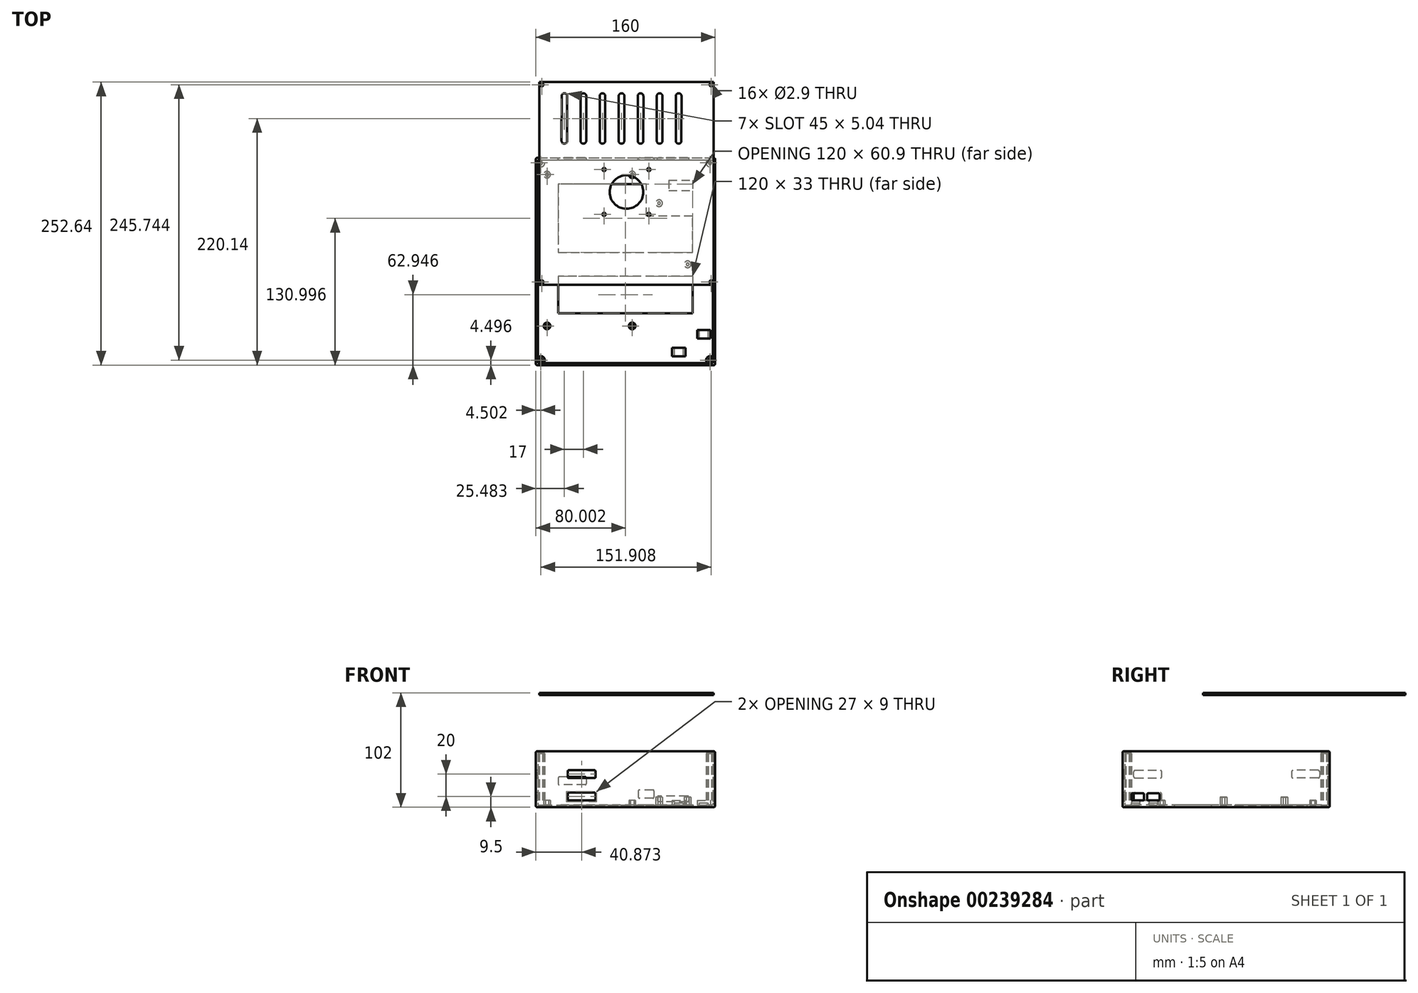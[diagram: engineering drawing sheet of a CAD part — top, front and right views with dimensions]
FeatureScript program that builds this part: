
annotation { "Feature Type Name" : "Feature", "Feature Type Description" : "" }
export const myFeature = defineFeature(function(context is Context, id is Id, definition is map)
    precondition{}
    {
        {
            assignVariable(context, id + "F0", {"name" : "mksPoleHeight", "anyValue" : 6});
        }
        {
            assignVariable(context, id + "F1", {"name" : "rpiPoleHeight", "anyValue" : 9});
        }
        {
            assignVariable(context, id + "F2", {"name" : "outerPoleHeight", "anyValue" : 48});
        }
        {
            var Q0;
            Q0=qCreatedBy(makeId("Top.planeOp"),FACE);
            var sketch = newSketch(context, id + "F3", { "sketchPlane" : qUnion([Q0])});
            skLineSegment(sketch, "E0.bottom", {"start": v(24.93, -36.84) * mm, "end": v(-51.07, -36.84) * mm});
            skLineSegment(sketch, "E0.top", {"start": v(24.93, 98.16) * mm, "end": v(-51.07, 98.16) * mm});
            skLineSegment(sketch, "E0.left", {"start": v(24.93, -36.84) * mm, "end": v(24.93, 98.16) * mm});
            skLineSegment(sketch, "E0.right", {"start": v(-51.07, -36.84) * mm, "end": v(-51.07, 98.16) * mm});
            skPoint(sketch, "E1", {"position": v(24.93, -36.84) * mm});
            skPoint(sketch, "E2", {"position": v(-51.07, -36.84) * mm});
            skPoint(sketch, "E3", {"position": v(24.93, 98.16) * mm});
            skPoint(sketch, "E4", {"position": v(-51.07, 98.16) * mm});
            skCircle(sketch, "E5", {"center": v(-51.07, 98.16) * mm, "radius": 3 * mm});
            skCircle(sketch, "E6", {"center": v(-51.07, -36.84) * mm, "radius": 3 * mm});
            skCircle(sketch, "E7", {"center": v(24.93, -36.84) * mm, "radius": 3 * mm});
            skCircle(sketch, "E8", {"center": v(24.93, 98.16) * mm, "radius": 3 * mm});
            skSolve(sketch);
        }
        {
            var Q0;
            {var subQ0=sQuery(id+"F3.wireOp",EDGE,"E7");var subQ1=sQuery(id+"F3.wireOp",EDGE,"E0.bottom");var subQ2=makeQuery(id+"F3.imprint","INTERSECT",VERTEX,{"derivedFrom":[subQ1,subQ0]});Q0=makeQuery(id+"F3.imprint","IMPRINT",FACE,{"disambiguationData":[TD([[makeQuery(id+"F3.imprint","IMPRINT",EDGE,{"disambiguationData":[TD([[subQ2,1.0]])],"derivedFrom":subQ1}),1.0]])]});}
            var Q1;
            {var subQ0=sQuery(id+"F3.wireOp",EDGE,"E7");var subQ1=sQuery(id+"F3.wireOp",EDGE,"E0.bottom");var subQ2=makeQuery(id+"F3.imprint","INTERSECT",VERTEX,{"derivedFrom":[subQ1,subQ0]});Q1=makeQuery(id+"F3.imprint","IMPRINT",FACE,{"disambiguationData":[TD([[makeQuery(id+"F3.imprint","IMPRINT",EDGE,{"disambiguationData":[TD([[subQ2,1.0]])],"derivedFrom":subQ1}),-1.0]])]});}
            var Q2;
            {var subQ0=sQuery(id+"F3.wireOp",EDGE,"E8");var subQ1=sQuery(id+"F3.wireOp",EDGE,"E0.top");var subQ2=makeQuery(id+"F3.imprint","INTERSECT",VERTEX,{"derivedFrom":[subQ1,subQ0]});Q2=makeQuery(id+"F3.imprint","IMPRINT",FACE,{"disambiguationData":[TD([[makeQuery(id+"F3.imprint","IMPRINT",EDGE,{"disambiguationData":[TD([[subQ2,1.0]])],"derivedFrom":subQ1}),1.0]])]});}
            var Q3;
            {var subQ0=sQuery(id+"F3.wireOp",EDGE,"E8");var subQ1=sQuery(id+"F3.wireOp",EDGE,"E0.top");var subQ2=makeQuery(id+"F3.imprint","INTERSECT",VERTEX,{"derivedFrom":[subQ1,subQ0]});Q3=makeQuery(id+"F3.imprint","IMPRINT",FACE,{"disambiguationData":[TD([[makeQuery(id+"F3.imprint","IMPRINT",EDGE,{"disambiguationData":[TD([[subQ2,1.0]])],"derivedFrom":subQ1}),-1.0]])]});}
            var Q4;
            {var subQ0=sQuery(id+"F3.wireOp",EDGE,"E5");var subQ1=sQuery(id+"F3.wireOp",EDGE,"E0.top");var subQ2=makeQuery(id+"F3.imprint","INTERSECT",VERTEX,{"derivedFrom":[subQ1,subQ0]});Q4=makeQuery(id+"F3.imprint","IMPRINT",FACE,{"disambiguationData":[TD([[makeQuery(id+"F3.imprint","IMPRINT",EDGE,{"disambiguationData":[TD([[subQ2,-1.0]])],"derivedFrom":subQ1}),-1.0]])]});}
            var Q5;
            {var subQ0=sQuery(id+"F3.wireOp",EDGE,"E5");var subQ1=sQuery(id+"F3.wireOp",EDGE,"E0.top");var subQ2=makeQuery(id+"F3.imprint","INTERSECT",VERTEX,{"derivedFrom":[subQ1,subQ0]});Q5=makeQuery(id+"F3.imprint","IMPRINT",FACE,{"disambiguationData":[TD([[makeQuery(id+"F3.imprint","IMPRINT",EDGE,{"disambiguationData":[TD([[subQ2,-1.0]])],"derivedFrom":subQ1}),1.0]])]});}
            var Q6;
            {var subQ0=sQuery(id+"F3.wireOp",EDGE,"E6");var subQ1=sQuery(id+"F3.wireOp",EDGE,"E0.bottom");var subQ2=makeQuery(id+"F3.imprint","INTERSECT",VERTEX,{"derivedFrom":[subQ1,subQ0]});Q6=makeQuery(id+"F3.imprint","IMPRINT",FACE,{"disambiguationData":[TD([[makeQuery(id+"F3.imprint","IMPRINT",EDGE,{"disambiguationData":[TD([[subQ2,-1.0]])],"derivedFrom":subQ1}),-1.0]])]});}
            var Q7;
            {var subQ0=sQuery(id+"F3.wireOp",EDGE,"E6");var subQ1=sQuery(id+"F3.wireOp",EDGE,"E0.bottom");var subQ2=makeQuery(id+"F3.imprint","INTERSECT",VERTEX,{"derivedFrom":[subQ1,subQ0]});Q7=makeQuery(id+"F3.imprint","IMPRINT",FACE,{"disambiguationData":[TD([[makeQuery(id+"F3.imprint","IMPRINT",EDGE,{"disambiguationData":[TD([[subQ2,-1.0]])],"derivedFrom":subQ1}),1.0]])]});}
            extrude(context, id + "F4", {"entities" : qUnion([Q0, Q1, Q2, Q3, Q4, Q5, Q6, Q7]), "depth" : getVariable(context, 'mksPoleHeight') * mm});
        }
        {
            var Q0;
            Q0=qCreatedBy(makeId("Top.planeOp"),FACE);
            var sketch = newSketch(context, id + "F5", { "sketchPlane" : qUnion([Q0])});
            skLineSegment(sketch, "E9.bottom", {"start": v(86.93, 13.16) * mm, "end": v(30.93, 13.16) * mm});
            skLineSegment(sketch, "E9.top", {"start": v(86.93, 98.16) * mm, "end": v(30.93, 98.16) * mm});
            skLineSegment(sketch, "E9.left", {"start": v(86.93, 13.16) * mm, "end": v(86.93, 98.16) * mm});
            skLineSegment(sketch, "E9.right", {"start": v(30.93, 13.16) * mm, "end": v(30.93, 98.16) * mm});
            skPoint(sketch, "E10", {"position": v(74.43, 18.16) * mm});
            skPoint(sketch, "E11", {"position": v(48.93, 72.66) * mm});
            skCircle(sketch, "E12", {"center": v(48.93, 72.66) * mm, "radius": 3 * mm});
            skCircle(sketch, "E13", {"center": v(74.43, 18.16) * mm, "radius": 3 * mm});
            skSolve(sketch);
        }
        {
            var Q0;
            Q0=makeQuery(id+"F5.imprint","IMPRINT",FACE,{"disambiguationData":[TD([[makeQuery(id+"F5.imprint","IMPRINT",EDGE,{"derivedFrom":sQuery(id+"F5.wireOp",EDGE,"E13")}),1.0]])]});
            var Q1;
            Q1=makeQuery(id+"F5.imprint","IMPRINT",FACE,{"disambiguationData":[TD([[makeQuery(id+"F5.imprint","IMPRINT",EDGE,{"derivedFrom":sQuery(id+"F5.wireOp",EDGE,"E12")}),1.0]])]});
            extrude(context, id + "F6", {"entities" : qUnion([Q0, Q1]), "depth" : getVariable(context, 'rpiPoleHeight') * mm});
        }
        {
            var Q0;
            Q0=qCreatedBy(makeId("Top.planeOp"),FACE);
            var sketch = newSketch(context, id + "F7", { "sketchPlane" : qUnion([Q0])});
            skLineSegment(sketch, "E14.bottom", {"start": v(-61.07, 113.16) * mm, "end": v(98.93, 113.16) * mm});
            skLineSegment(sketch, "E14.top", {"start": v(-61.07, -71.84) * mm, "end": v(98.93, -71.84) * mm});
            skLineSegment(sketch, "E14.left", {"start": v(-61.07, 113.16) * mm, "end": v(-61.07, -71.84) * mm});
            skLineSegment(sketch, "E14.right", {"start": v(98.93, 113.16) * mm, "end": v(98.93, -71.84) * mm});
            skPoint(sketch, "E15", {"position": v(-56.57, 108.66) * mm});
            skPoint(sketch, "E16", {"position": v(-56.57, -67.34) * mm});
            skPoint(sketch, "E17", {"position": v(94.43, -67.34) * mm});
            skPoint(sketch, "E18", {"position": v(94.43, 108.66) * mm});
            skCircle(sketch, "E19", {"center": v(-56.57, -67.34) * mm, "radius": 3.5 * mm});
            skCircle(sketch, "E20", {"center": v(94.43, -67.34) * mm, "radius": 3.5 * mm});
            skCircle(sketch, "E21", {"center": v(94.43, 108.66) * mm, "radius": 3.5 * mm});
            skCircle(sketch, "E22", {"center": v(-56.57, 108.66) * mm, "radius": 3.5 * mm});
            skSolve(sketch);
        }
        {
            var Q0;
            Q0=makeQuery(id+"F7.imprint","IMPRINT",FACE,{"disambiguationData":[TD([[makeQuery(id+"F7.imprint","IMPRINT",EDGE,{"derivedFrom":sQuery(id+"F7.wireOp",EDGE,"E14.bottom")}),-1.0]])]});
            var Q1;
            Q1=makeQuery(id+"F7.imprint","IMPRINT",FACE,{"disambiguationData":[TD([[makeQuery(id+"F7.imprint","IMPRINT",EDGE,{"derivedFrom":sQuery(id+"F7.wireOp",EDGE,"E22")}),1.0]])]});
            var Q2;
            Q2=makeQuery(id+"F7.imprint","IMPRINT",FACE,{"disambiguationData":[TD([[makeQuery(id+"F7.imprint","IMPRINT",EDGE,{"derivedFrom":sQuery(id+"F7.wireOp",EDGE,"E19")}),1.0]])]});
            var Q3;
            Q3=makeQuery(id+"F7.imprint","IMPRINT",FACE,{"disambiguationData":[TD([[makeQuery(id+"F7.imprint","IMPRINT",EDGE,{"derivedFrom":sQuery(id+"F7.wireOp",EDGE,"E20")}),1.0]])]});
            var Q4;
            Q4=makeQuery(id+"F7.imprint","IMPRINT",FACE,{"disambiguationData":[TD([[makeQuery(id+"F7.imprint","IMPRINT",EDGE,{"derivedFrom":sQuery(id+"F7.wireOp",EDGE,"E21")}),1.0]])]});
            extrude(context, id + "F8", {"entities" : qUnion([Q0, Q1, Q2, Q3, Q4]), "depth" : 50 * mm});
        }
        {
            var Q0;
            Q0=makeQuery(id+"F8.opExtrude","CAP_FACE",FACE,{"disambiguationData":[OSD([sQuery(id+"F7.wireOp",EDGE,"E14.bottom"),sQuery(id+"F7.wireOp",EDGE,"E14.top"),sQuery(id+"F7.wireOp",EDGE,"E14.left"),sQuery(id+"F7.wireOp",EDGE,"E14.right")])],"isStart":false});
            shell(context, id + "F9", {"entities" : qUnion([Q0]), "thickness" : 2 * mm});
        }
        {
            var Q0;
            Q0=makeQuery(id+"F7.imprint","IMPRINT",FACE,{"disambiguationData":[TD([[makeQuery(id+"F7.imprint","IMPRINT",EDGE,{"derivedFrom":sQuery(id+"F7.wireOp",EDGE,"E19")}),1.0]])]});
            var Q1;
            Q1=makeQuery(id+"F7.imprint","IMPRINT",FACE,{"disambiguationData":[TD([[makeQuery(id+"F7.imprint","IMPRINT",EDGE,{"derivedFrom":sQuery(id+"F7.wireOp",EDGE,"E20")}),1.0]])]});
            var Q2;
            Q2=makeQuery(id+"F7.imprint","IMPRINT",FACE,{"disambiguationData":[TD([[makeQuery(id+"F7.imprint","IMPRINT",EDGE,{"derivedFrom":sQuery(id+"F7.wireOp",EDGE,"E21")}),1.0]])]});
            var Q3;
            Q3=makeQuery(id+"F7.imprint","IMPRINT",FACE,{"disambiguationData":[TD([[makeQuery(id+"F7.imprint","IMPRINT",EDGE,{"derivedFrom":sQuery(id+"F7.wireOp",EDGE,"E22")}),1.0]])]});
            var Q4;
            Q4=sQuery(id+"F7.wireOp",EDGE,"E19");
            var Q5;
            Q5=sQuery(id+"F7.wireOp",EDGE,"E20");
            var Q6;
            Q6=sQuery(id+"F7.wireOp",EDGE,"E21");
            var Q7;
            Q7=sQuery(id+"F7.wireOp",EDGE,"E22");
            extrude(context, id + "F10", {"entities" : qUnion([Q0, Q1, Q2, Q3]), "surfaceEntities" : qUnion([Q4, Q5, Q6, Q7]), "depth" : (getVariable(context, 'outerPoleHeight')) * mm});
        }
        {
            var Q0;
            Q0=makeQuery(id+"F8.opExtrude","CAP_FACE",FACE,{"disambiguationData":[OSD([sQuery(id+"F7.wireOp",EDGE,"E14.bottom"),sQuery(id+"F7.wireOp",EDGE,"E14.top"),sQuery(id+"F7.wireOp",EDGE,"E14.left"),sQuery(id+"F7.wireOp",EDGE,"E14.right")])],"isStart":false});
            cPlane(context, id + "F11", {"entities" : qUnion([Q0]), "cplaneType" : CPlaneType.OFFSET, "offset" : 0 * mm, "width" : 150 * mm, "height" : 150 * mm});
        }
        {
            var Q0;
            Q0=qCreatedBy(id+"F11.planeOp",FACE);
            var sketch = newSketch(context, id + "F12", { "sketchPlane" : qUnion([Q0])});
            skLineSegment(sketch, "E23.bottom", {"start": v(-59.07, 111.16) * mm, "end": v(96.93, 111.16) * mm});
            skLineSegment(sketch, "E23.top", {"start": v(-59.07, -69.84) * mm, "end": v(96.93, -69.84) * mm});
            skLineSegment(sketch, "E23.left", {"start": v(-59.07, 111.16) * mm, "end": v(-59.07, -69.84) * mm});
            skLineSegment(sketch, "E23.right", {"start": v(96.93, 111.16) * mm, "end": v(96.93, -69.84) * mm});
            skSolve(sketch);
        }
        {
            var Q0;
            Q0=makeQuery(id+"F12.imprint","IMPRINT",FACE,{"disambiguationData":[TD([[makeQuery(id+"F12.imprint","IMPRINT",EDGE,{"derivedFrom":sQuery(id+"F12.wireOp",EDGE,"E23.bottom")}),-1.0]])]});
            extrude(context, id + "F13", {"entities" : qUnion([Q0]), "operationType" : NewBodyOperationType.REMOVE, "oppositeDirection" : true, "depth" : 2 * mm});
        }
        {
            var Q0;
            Q0=makeQuery(id+"F4.opExtrude","SWEPT_BODY",BODY,{"disambiguationData":[OSD([sQuery(id+"F3.wireOp",EDGE,"E5")])]});
            var Q1;
            Q1=makeQuery(id+"F4.opExtrude","SWEPT_BODY",BODY,{"disambiguationData":[OSD([sQuery(id+"F3.wireOp",EDGE,"E6")])]});
            var Q2;
            Q2=makeQuery(id+"F4.opExtrude","SWEPT_BODY",BODY,{"disambiguationData":[OSD([sQuery(id+"F3.wireOp",EDGE,"E7")])]});
            var Q3;
            Q3=makeQuery(id+"F4.opExtrude","SWEPT_BODY",BODY,{"disambiguationData":[OSD([sQuery(id+"F3.wireOp",EDGE,"E8")])]});
            var Q4;
            Q4=makeQuery(id+"F6.opExtrude","SWEPT_BODY",BODY,{"disambiguationData":[OSD([sQuery(id+"F5.wireOp",EDGE,"E12")])]});
            var Q5;
            Q5=makeQuery(id+"F6.opExtrude","SWEPT_BODY",BODY,{"disambiguationData":[OSD([sQuery(id+"F5.wireOp",EDGE,"E13")])]});
            var Q6;
            Q6=makeQuery(id+"F8.opExtrude","SWEPT_BODY",BODY,{"disambiguationData":[OSD([sQuery(id+"F7.wireOp",EDGE,"E14.bottom"),sQuery(id+"F7.wireOp",EDGE,"E14.top"),sQuery(id+"F7.wireOp",EDGE,"E14.left"),sQuery(id+"F7.wireOp",EDGE,"E14.right")])]});
            var Q7;
            Q7=makeQuery(id+"F10.opExtrude","SWEPT_BODY",BODY,{"disambiguationData":[OSD([sQuery(id+"F7.wireOp",EDGE,"E19")])]});
            var Q8;
            Q8=makeQuery(id+"F10.opExtrude","SWEPT_BODY",BODY,{"disambiguationData":[OSD([sQuery(id+"F7.wireOp",EDGE,"E20")])]});
            var Q9;
            Q9=makeQuery(id+"F10.opExtrude","SWEPT_BODY",BODY,{"disambiguationData":[OSD([sQuery(id+"F7.wireOp",EDGE,"E21")])]});
            var Q10;
            Q10=makeQuery(id+"F10.opExtrude","SWEPT_BODY",BODY,{"disambiguationData":[OSD([sQuery(id+"F7.wireOp",EDGE,"E22")])]});
            booleanBodies(context, id + "F14", {"operationType" : BooleanOperationType.UNION, "tools" : qUnion([Q0, Q1, Q2, Q3, Q4, Q5, Q6, Q7, Q8, Q9, Q10])});
        }
        {
            var Q0;
            Q0=sQuery(id+"F7.wireOp",VERTEX,"E16");
            var Q1;
            Q1=sQuery(id+"F7.wireOp",VERTEX,"E15");
            var Q2;
            Q2=sQuery(id+"F7.wireOp",VERTEX,"E18");
            var Q3;
            Q3=sQuery(id+"F7.wireOp",VERTEX,"E17");
            var Q4;
            Q4=sQuery(id+"F3.wireOp",VERTEX,"E3");
            var Q5;
            Q5=sQuery(id+"F3.wireOp",VERTEX,"E4");
            var Q6;
            Q6=sQuery(id+"F3.wireOp",VERTEX,"E2");
            var Q7;
            Q7=sQuery(id+"F3.wireOp",VERTEX,"E1");
            var Q8;
            Q8=makeQuery(id+"F4.opExtrude","SWEPT_BODY",BODY,{"disambiguationData":[OSD([sQuery(id+"F3.wireOp",EDGE,"E5")])]});
            hole(context, id + "F15", {"style" : HoleStyle.SIMPLE, "endStyle" : HoleEndStyle.THROUGH, "oppositeDirection" : true, "holeDiameter" : 2.9 * mm, "tappedDepth" : 12 * mm, "tapClearance" : 3, "startFromSketch" : true, "locations" : qUnion([Q0, Q1, Q2, Q3, Q4, Q5, Q6, Q7]), "scope" : qUnion([Q8])});
        }
        {
            var Q0;
            Q0=qCreatedBy(id+"F11.planeOp",FACE);
            cPlane(context, id + "F16", {"entities" : qUnion([Q0]), "cplaneType" : CPlaneType.OFFSET, "offset" : 50 * mm, "width" : 150 * mm, "height" : 150 * mm});
        }
        {
            var Q0;
            Q0=qCreatedBy(id+"F16.planeOp",FACE);
            var sketch = newSketch(context, id + "F17", { "sketchPlane" : qUnion([Q0])});
            skLineSegment(sketch, "E24.bottom", {"start": v(-58.06, 180.8) * mm, "end": v(97.74, 180.8) * mm});
            skLineSegment(sketch, "E24.top", {"start": v(-58.06, 0) * mm, "end": v(97.74, 0) * mm});
            skLineSegment(sketch, "E24.left", {"start": v(-58.06, 180.8) * mm, "end": v(-58.06, 0) * mm});
            skLineSegment(sketch, "E24.right", {"start": v(97.74, 180.8) * mm, "end": v(97.74, 0) * mm});
            skPoint(sketch, "E25", {"position": v(-55.66, 178.4) * mm});
            skPoint(sketch, "E26", {"position": v(95.34, 178.4) * mm});
            skPoint(sketch, "E27", {"position": v(95.34, 2.4) * mm});
            skPoint(sketch, "E28", {"position": v(-55.66, 2.4) * mm});
            skCircle(sketch, "E29", {"center": v(-55.66, 178.4) * mm, "radius": 1.45 * mm});
            skCircle(sketch, "E30", {"center": v(95.34, 178.4) * mm, "radius": 1.45 * mm});
            skCircle(sketch, "E31", {"center": v(95.34, 2.4) * mm, "radius": 1.45 * mm});
            skCircle(sketch, "E32", {"center": v(-55.66, 2.4) * mm, "radius": 1.45 * mm});
            skArc(sketch, "E33.0.startCap", {"start": v(-38.06, 168.3) * mm, "mid": v(-35.56, 170.8) * mm, "end": v(-33.07, 168.3) * mm});
            skArc(sketch, "E33.0.endCap", {"start": v(-33.1, 128.3) * mm, "mid": v(-35.61, 125.8) * mm, "end": v(-38.1, 128.3) * mm});
            skLineSegment(sketch, "E33.0.left", {"start": v(-33.07, 168.3) * mm, "end": v(-33.1, 128.3) * mm});
            skLineSegment(sketch, "E33.0.right", {"start": v(-38.06, 168.3) * mm, "end": v(-38.1, 128.3) * mm});
            skArc(sketch, "E34.0.startCap", {"start": v(-21.06, 168.3) * mm, "mid": v(-18.56, 170.8) * mm, "end": v(-16.06, 168.3) * mm});
            skArc(sketch, "E34.0.endCap", {"start": v(-16.1, 128.3) * mm, "mid": v(-18.61, 125.8) * mm, "end": v(-21.1, 128.3) * mm});
            skLineSegment(sketch, "E34.0.left", {"start": v(-16.06, 168.3) * mm, "end": v(-16.1, 128.3) * mm});
            skLineSegment(sketch, "E34.0.right", {"start": v(-21.06, 168.3) * mm, "end": v(-21.1, 128.3) * mm});
            skArc(sketch, "E35.0.startCap", {"start": v(-4.06, 168.3) * mm, "mid": v(-1.56, 170.8) * mm, "end": v(0.94, 168.3) * mm});
            skArc(sketch, "E35.0.endCap", {"start": v(0.9, 128.3) * mm, "mid": v(-1.61, 125.8) * mm, "end": v(-4.1, 128.3) * mm});
            skLineSegment(sketch, "E35.0.left", {"start": v(0.94, 168.3) * mm, "end": v(0.9, 128.3) * mm});
            skLineSegment(sketch, "E35.0.right", {"start": v(-4.06, 168.3) * mm, "end": v(-4.1, 128.3) * mm});
            skArc(sketch, "E36.0.startCap", {"start": v(12.94, 168.3) * mm, "mid": v(15.44, 170.8) * mm, "end": v(17.94, 168.3) * mm});
            skArc(sketch, "E36.0.endCap", {"start": v(17.9, 128.3) * mm, "mid": v(15.39, 125.8) * mm, "end": v(12.9, 128.3) * mm});
            skLineSegment(sketch, "E36.0.left", {"start": v(17.94, 168.3) * mm, "end": v(17.9, 128.3) * mm});
            skLineSegment(sketch, "E36.0.right", {"start": v(12.94, 168.3) * mm, "end": v(12.9, 128.3) * mm});
            skArc(sketch, "E37.0.startCap", {"start": v(29.94, 168.3) * mm, "mid": v(32.44, 170.8) * mm, "end": v(34.94, 168.3) * mm});
            skArc(sketch, "E37.0.endCap", {"start": v(34.9, 128.3) * mm, "mid": v(32.39, 125.8) * mm, "end": v(29.9, 128.3) * mm});
            skLineSegment(sketch, "E37.0.left", {"start": v(34.94, 168.3) * mm, "end": v(34.9, 128.3) * mm});
            skLineSegment(sketch, "E37.0.right", {"start": v(29.94, 168.3) * mm, "end": v(29.9, 128.3) * mm});
            skArc(sketch, "E38.0.startCap", {"start": v(46.94, 168.3) * mm, "mid": v(49.44, 170.8) * mm, "end": v(51.94, 168.3) * mm});
            skArc(sketch, "E38.0.endCap", {"start": v(51.9, 128.3) * mm, "mid": v(49.39, 125.8) * mm, "end": v(46.9, 128.3) * mm});
            skLineSegment(sketch, "E38.0.left", {"start": v(51.94, 168.3) * mm, "end": v(51.9, 128.3) * mm});
            skLineSegment(sketch, "E38.0.right", {"start": v(46.94, 168.3) * mm, "end": v(46.9, 128.3) * mm});
            skArc(sketch, "E39.0.startCap", {"start": v(63.94, 168.3) * mm, "mid": v(66.44, 170.8) * mm, "end": v(68.94, 168.3) * mm});
            skArc(sketch, "E39.0.endCap", {"start": v(68.9, 128.3) * mm, "mid": v(66.39, 125.8) * mm, "end": v(63.9, 128.3) * mm});
            skLineSegment(sketch, "E39.0.left", {"start": v(68.94, 168.3) * mm, "end": v(68.9, 128.3) * mm});
            skLineSegment(sketch, "E39.0.right", {"start": v(63.94, 168.3) * mm, "end": v(63.9, 128.3) * mm});
            skPoint(sketch, "E40", {"position": v(19.84, 82.67) * mm});
            skCircle(sketch, "E41", {"center": v(19.84, 82.67) * mm, "radius": 15 * mm});
            skLineSegment(sketch, "E42.bottom", {"start": v(39.84, 102.67) * mm, "end": v(-0.16, 102.67) * mm});
            skLineSegment(sketch, "E42.top", {"start": v(39.84, 62.67) * mm, "end": v(-0.16, 62.67) * mm});
            skLineSegment(sketch, "E42.left", {"start": v(39.84, 102.67) * mm, "end": v(39.84, 62.67) * mm});
            skLineSegment(sketch, "E42.right", {"start": v(-0.16, 102.67) * mm, "end": v(-0.16, 62.67) * mm});
            skCircle(sketch, "E43", {"center": v(-0.16, 102.67) * mm, "radius": 1.45 * mm});
            skCircle(sketch, "E44", {"center": v(-0.16, 62.67) * mm, "radius": 1.45 * mm});
            skCircle(sketch, "E45", {"center": v(39.84, 102.67) * mm, "radius": 1.45 * mm});
            skCircle(sketch, "E46", {"center": v(39.84, 62.67) * mm, "radius": 1.45 * mm});
            skSolve(sketch);
        }
        {
            var Q0;
            Q0=makeQuery(id+"F17.imprint","IMPRINT",FACE,{"disambiguationData":[TD([[makeQuery(id+"F17.imprint","IMPRINT",EDGE,{"derivedFrom":sQuery(id+"F17.wireOp",EDGE,"E24.bottom")}),-1.0]])]});
            var Q1;
            Q1=makeQuery(id+"F17.imprint","IMPRINT",FACE,{"disambiguationData":[TD([[makeQuery(id+"F17.imprint","IMPRINT",EDGE,{"derivedFrom":sQuery(id+"F17.wireOp",EDGE,"E41")}),-1.0]])]});
            extrude(context, id + "F18", {"entities" : qUnion([Q0, Q1]), "depth" : 2 * mm});
        }
        {
            var Q0;
            Q0=makeQuery(id+"F8.opExtrude","SWEPT_FACE",FACE,{"disambiguationData":[OSD([sQuery(id+"F7.wireOp",EDGE,"E14.left")])]});
            var sketch = newSketch(context, id + "F19", { "sketchPlane" : qUnion([Q0])});
            skLineSegment(sketch, "E47.bottom", {"start": v(-79.13, 26) * mm, "end": v(-104.13, 26) * mm});
            skLineSegment(sketch, "E47.top", {"start": v(-79.13, 33) * mm, "end": v(-104.13, 33) * mm});
            skLineSegment(sketch, "E47.left", {"start": v(-79.13, 26) * mm, "end": v(-79.13, 33) * mm});
            skLineSegment(sketch, "E47.right", {"start": v(-104.13, 26) * mm, "end": v(-104.13, 33) * mm});
            skLineSegment(sketch, "E48.bottom", {"start": v(36.84, 33) * mm, "end": v(61.84, 33) * mm});
            skLineSegment(sketch, "E48.top", {"start": v(36.84, 26) * mm, "end": v(61.84, 26) * mm});
            skLineSegment(sketch, "E48.left", {"start": v(36.84, 33) * mm, "end": v(36.84, 26) * mm});
            skLineSegment(sketch, "E48.right", {"start": v(61.84, 33) * mm, "end": v(61.84, 26) * mm});
            skLineSegment(sketch, "E49.bottom", {"start": v(36.84, 13) * mm, "end": v(61.84, 13) * mm});
            skLineSegment(sketch, "E49.top", {"start": v(36.84, 6) * mm, "end": v(61.84, 6) * mm});
            skLineSegment(sketch, "E49.left", {"start": v(36.84, 13) * mm, "end": v(36.84, 6) * mm});
            skLineSegment(sketch, "E49.right", {"start": v(61.84, 13) * mm, "end": v(61.84, 6) * mm});
            skSolve(sketch);
        }
        {
            var Q0;
            Q0=makeQuery(id+"F19.imprint","IMPRINT",FACE,{"disambiguationData":[TD([[makeQuery(id+"F19.imprint","IMPRINT",EDGE,{"derivedFrom":sQuery(id+"F19.wireOp",EDGE,"E48.bottom")}),-1.0]])]});
            var Q1;
            Q1=makeQuery(id+"F19.imprint","IMPRINT",FACE,{"disambiguationData":[TD([[makeQuery(id+"F19.imprint","IMPRINT",EDGE,{"derivedFrom":sQuery(id+"F19.wireOp",EDGE,"d830608d-766a-4a5a-9b51-aef29d65a364.bottom")}),-1.0]])]});
            var Q2;
            Q2=makeQuery(id+"F19.imprint","IMPRINT",FACE,{"disambiguationData":[TD([[makeQuery(id+"F19.imprint","IMPRINT",EDGE,{"derivedFrom":sQuery(id+"F19.wireOp",EDGE,"E49.bottom")}),-1.0]])]});
            var Q3;
            Q3=makeQuery(id+"F19.imprint","IMPRINT",FACE,{"disambiguationData":[TD([[makeQuery(id+"F19.imprint","IMPRINT",EDGE,{"derivedFrom":sQuery(id+"F19.wireOp",EDGE,"E47.bottom")}),-1.0]])]});
            extrude(context, id + "F20", {"entities" : qUnion([Q0, Q1, Q2, Q3]), "operationType" : NewBodyOperationType.REMOVE, "oppositeDirection" : true, "depth" : 5 * mm});
        }
        {
            var Q0;
            Q0=makeQuery(id+"F8.opExtrude","SWEPT_FACE",FACE,{"disambiguationData":[OSD([sQuery(id+"F7.wireOp",EDGE,"E14.left")])]});
            var Q1;
            Q1=makeQuery(id+"F8.opExtrude","SWEPT_FACE",FACE,{"disambiguationData":[OSD([sQuery(id+"F7.wireOp",EDGE,"E14.bottom")])]});
            var Q2;
            Q2=makeQuery(id+"F8.opExtrude","SWEPT_FACE",FACE,{"disambiguationData":[OSD([sQuery(id+"F7.wireOp",EDGE,"E14.right")])]});
            var Q3;
            Q3=makeQuery(id+"F8.opExtrude","SWEPT_FACE",FACE,{"disambiguationData":[OSD([sQuery(id+"F7.wireOp",EDGE,"E14.top")])]});
            var Q4;
            Q4=makeQuery(id+"F20.boolean.opBoolean","COPY",EDGE,{"derivedFrom":makeQuery(id+"F20.opExtrude","SWEPT_EDGE",EDGE,{"disambiguationData":[OSD([sQuery(id+"F19.wireOp",EDGE,"d830608d-766a-4a5a-9b51-aef29d65a364.top"),sQuery(id+"F19.wireOp",EDGE,"d830608d-766a-4a5a-9b51-aef29d65a364.left")])]})});
            var Q5;
            Q5=makeQuery(id+"F20.boolean.opBoolean","COPY",EDGE,{"derivedFrom":makeQuery(id+"F20.opExtrude","SWEPT_EDGE",EDGE,{"disambiguationData":[OSD([sQuery(id+"F19.wireOp",EDGE,"E47.bottom"),sQuery(id+"F19.wireOp",EDGE,"E47.right")])]})});
            var Q6;
            Q6=makeQuery(id+"F20.boolean.opBoolean","COPY",EDGE,{"derivedFrom":makeQuery(id+"F20.opExtrude","SWEPT_EDGE",EDGE,{"disambiguationData":[OSD([sQuery(id+"F19.wireOp",EDGE,"E48.top"),sQuery(id+"F19.wireOp",EDGE,"E48.left")])]})});
            var Q7;
            Q7=makeQuery(id+"F20.boolean.opBoolean","COPY",EDGE,{"derivedFrom":makeQuery(id+"F20.opExtrude","SWEPT_EDGE",EDGE,{"disambiguationData":[OSD([sQuery(id+"F19.wireOp",EDGE,"E49.top"),sQuery(id+"F19.wireOp",EDGE,"E49.left")])]})});
            var Q8;
            Q8=makeQuery(id+"F20.boolean.opBoolean","COPY",EDGE,{"derivedFrom":makeQuery(id+"F20.opExtrude","SWEPT_EDGE",EDGE,{"disambiguationData":[OSD([sQuery(id+"F19.wireOp",EDGE,"E47.bottom"),sQuery(id+"F19.wireOp",EDGE,"E47.left")])]})});
            var Q9;
            Q9=makeQuery(id+"F20.boolean.opBoolean","COPY",EDGE,{"derivedFrom":makeQuery(id+"F20.opExtrude","SWEPT_EDGE",EDGE,{"disambiguationData":[OSD([sQuery(id+"F19.wireOp",EDGE,"d830608d-766a-4a5a-9b51-aef29d65a364.top"),sQuery(id+"F19.wireOp",EDGE,"d830608d-766a-4a5a-9b51-aef29d65a364.right")])]})});
            var Q10;
            Q10=makeQuery(id+"F20.boolean.opBoolean","COPY",EDGE,{"derivedFrom":makeQuery(id+"F20.opExtrude","SWEPT_EDGE",EDGE,{"disambiguationData":[OSD([sQuery(id+"F19.wireOp",EDGE,"E49.top"),sQuery(id+"F19.wireOp",EDGE,"E49.right")])]})});
            var Q11;
            Q11=makeQuery(id+"F20.boolean.opBoolean","COPY",EDGE,{"derivedFrom":makeQuery(id+"F20.opExtrude","SWEPT_EDGE",EDGE,{"disambiguationData":[OSD([sQuery(id+"F19.wireOp",EDGE,"E48.top"),sQuery(id+"F19.wireOp",EDGE,"E48.right")])]})});
            var Q12;
            Q12=makeQuery(id+"F20.boolean.opBoolean","COPY",EDGE,{"derivedFrom":makeQuery(id+"F20.opExtrude","SWEPT_EDGE",EDGE,{"disambiguationData":[OSD([sQuery(id+"F19.wireOp",EDGE,"E49.bottom"),sQuery(id+"F19.wireOp",EDGE,"E49.right")])]})});
            var Q13;
            Q13=makeQuery(id+"F20.boolean.opBoolean","COPY",EDGE,{"derivedFrom":makeQuery(id+"F20.opExtrude","SWEPT_EDGE",EDGE,{"disambiguationData":[OSD([sQuery(id+"F19.wireOp",EDGE,"d830608d-766a-4a5a-9b51-aef29d65a364.bottom"),sQuery(id+"F19.wireOp",EDGE,"d830608d-766a-4a5a-9b51-aef29d65a364.right")])]})});
            var Q14;
            Q14=makeQuery(id+"F20.boolean.opBoolean","COPY",EDGE,{"derivedFrom":makeQuery(id+"F20.opExtrude","SWEPT_EDGE",EDGE,{"disambiguationData":[OSD([sQuery(id+"F19.wireOp",EDGE,"E47.top"),sQuery(id+"F19.wireOp",EDGE,"E47.left")])]})});
            var Q15;
            Q15=makeQuery(id+"F20.boolean.opBoolean","COPY",EDGE,{"derivedFrom":makeQuery(id+"F20.opExtrude","SWEPT_EDGE",EDGE,{"disambiguationData":[OSD([sQuery(id+"F19.wireOp",EDGE,"E48.bottom"),sQuery(id+"F19.wireOp",EDGE,"E48.right")])]})});
            var Q16;
            Q16=makeQuery(id+"F20.boolean.opBoolean","COPY",EDGE,{"derivedFrom":makeQuery(id+"F20.opExtrude","SWEPT_EDGE",EDGE,{"disambiguationData":[OSD([sQuery(id+"F19.wireOp",EDGE,"E48.bottom"),sQuery(id+"F19.wireOp",EDGE,"E48.left")])]})});
            var Q17;
            Q17=makeQuery(id+"F20.boolean.opBoolean","COPY",EDGE,{"derivedFrom":makeQuery(id+"F20.opExtrude","SWEPT_EDGE",EDGE,{"disambiguationData":[OSD([sQuery(id+"F19.wireOp",EDGE,"E49.bottom"),sQuery(id+"F19.wireOp",EDGE,"E49.left")])]})});
            var Q18;
            Q18=makeQuery(id+"F20.boolean.opBoolean","COPY",EDGE,{"derivedFrom":makeQuery(id+"F20.opExtrude","SWEPT_EDGE",EDGE,{"disambiguationData":[OSD([sQuery(id+"F19.wireOp",EDGE,"d830608d-766a-4a5a-9b51-aef29d65a364.bottom"),sQuery(id+"F19.wireOp",EDGE,"d830608d-766a-4a5a-9b51-aef29d65a364.left")])]})});
            var Q19;
            Q19=makeQuery(id+"F20.boolean.opBoolean","COPY",EDGE,{"derivedFrom":makeQuery(id+"F20.opExtrude","SWEPT_EDGE",EDGE,{"disambiguationData":[OSD([sQuery(id+"F19.wireOp",EDGE,"E47.top"),sQuery(id+"F19.wireOp",EDGE,"E47.right")])]})});
            fillet(context, id + "F21", {"entities" : qUnion([Q0, Q1, Q2, Q3, Q4, Q5, Q6, Q7, Q8, Q9, Q10, Q11, Q12, Q13, Q14, Q15, Q16, Q17, Q18, Q19]), "radius" : 1.3 * mm, "tangentPropagation" : true, "allowEdgeOverflow" : false});
        }
        {
            var Q0;
            Q0=makeQuery(id+"F8.opExtrude","SWEPT_FACE",FACE,{"disambiguationData":[OSD([sQuery(id+"F7.wireOp",EDGE,"E14.top")])]});
            var sketch = newSketch(context, id + "F22", { "sketchPlane" : qUnion([Q0])});
            skLineSegment(sketch, "E50.bottom", {"start": v(-32.7, 33) * mm, "end": v(-7.7, 33) * mm});
            skLineSegment(sketch, "E50.top", {"start": v(-32.7, 26) * mm, "end": v(-7.7, 26) * mm});
            skLineSegment(sketch, "E50.left", {"start": v(-32.7, 33) * mm, "end": v(-32.7, 26) * mm});
            skLineSegment(sketch, "E50.right", {"start": v(-7.7, 33) * mm, "end": v(-7.7, 26) * mm});
            skLineSegment(sketch, "E51.bottom", {"start": v(-32.7, 13) * mm, "end": v(-7.7, 13) * mm});
            skLineSegment(sketch, "E51.top", {"start": v(-32.7, 6) * mm, "end": v(-7.7, 6) * mm});
            skLineSegment(sketch, "E51.left", {"start": v(-32.7, 13) * mm, "end": v(-32.7, 6) * mm});
            skLineSegment(sketch, "E51.right", {"start": v(-7.7, 13) * mm, "end": v(-7.7, 6) * mm});
            skSolve(sketch);
        }
        {
            var Q0;
            Q0 = qSketchRegion(id + "F22", true);
            extrude(context, id + "F23", {"entities" : qUnion([Q0]), "operationType" : NewBodyOperationType.REMOVE, "oppositeDirection" : true, "depth" : 3 * mm});
        }
        {
            var Q0;
            Q0=makeQuery(id+"F8.opExtrude","SWEPT_FACE",FACE,{"disambiguationData":[OSD([sQuery(id+"F7.wireOp",EDGE,"E14.bottom")])]});
            var sketch = newSketch(context, id + "F24", { "sketchPlane" : qUnion([Q0])});
            skLineSegment(sketch, "E52.bottom", {"start": v(-44.43, 15.5) * mm, "end": v(-30.43, 15.5) * mm});
            skLineSegment(sketch, "E52.top", {"start": v(-44.43, 8) * mm, "end": v(-30.43, 8) * mm});
            skLineSegment(sketch, "E52.left", {"start": v(-44.43, 15.5) * mm, "end": v(-44.43, 8) * mm});
            skLineSegment(sketch, "E52.right", {"start": v(-30.43, 15.5) * mm, "end": v(-30.43, 8) * mm});
            skLineSegment(sketch, "E53.bottom", {"start": v(16.07, 27) * mm, "end": v(41.07, 27) * mm});
            skLineSegment(sketch, "E53.top", {"start": v(16.07, 20) * mm, "end": v(41.07, 20) * mm});
            skLineSegment(sketch, "E53.left", {"start": v(16.07, 27) * mm, "end": v(16.07, 20) * mm});
            skLineSegment(sketch, "E53.right", {"start": v(41.07, 27) * mm, "end": v(41.07, 20) * mm});
            skLineSegment(sketch, "E54.bottom", {"start": v(-75.43, 10) * mm, "end": v(-47.43, 10) * mm});
            skLineSegment(sketch, "E54.top", {"start": v(-75.43, 5) * mm, "end": v(-47.43, 5) * mm});
            skLineSegment(sketch, "E54.left", {"start": v(-75.43, 10) * mm, "end": v(-75.43, 5) * mm});
            skLineSegment(sketch, "E54.right", {"start": v(-47.43, 10) * mm, "end": v(-47.43, 5) * mm});
            skSolve(sketch);
        }
        {
            var Q0;
            Q0=makeQuery(id+"F8.opExtrude","SWEPT_FACE",FACE,{"disambiguationData":[OSD([sQuery(id+"F7.wireOp",EDGE,"E14.right")])]});
            var sketch = newSketch(context, id + "F25", { "sketchPlane" : qUnion([Q0])});
            skLineSegment(sketch, "E55.bottom", {"start": v(-63.64, 12.5) * mm, "end": v(-52.64, 12.5) * mm});
            skLineSegment(sketch, "E55.top", {"start": v(-63.64, 6) * mm, "end": v(-52.64, 6) * mm});
            skLineSegment(sketch, "E55.left", {"start": v(-63.64, 12.5) * mm, "end": v(-63.64, 6) * mm});
            skLineSegment(sketch, "E55.right", {"start": v(-52.64, 12.5) * mm, "end": v(-52.64, 6) * mm});
            skLineSegment(sketch, "E56.bottom", {"start": v(-49.84, 12.5) * mm, "end": v(-38.84, 12.5) * mm});
            skLineSegment(sketch, "E56.top", {"start": v(-49.84, 6) * mm, "end": v(-38.84, 6) * mm});
            skLineSegment(sketch, "E56.left", {"start": v(-49.84, 12.5) * mm, "end": v(-49.84, 6) * mm});
            skLineSegment(sketch, "E56.right", {"start": v(-38.84, 12.5) * mm, "end": v(-38.84, 6) * mm});
            skSolve(sketch);
        }
        {
            var Q0;
            Q0=makeQuery(id+"F25.imprint","IMPRINT",FACE,{"disambiguationData":[TD([[makeQuery(id+"F25.imprint","IMPRINT",EDGE,{"derivedFrom":sQuery(id+"F25.wireOp",EDGE,"E55.bottom")}),-1.0]])]});
            var Q1;
            Q1=makeQuery(id+"F25.imprint","IMPRINT",FACE,{"disambiguationData":[TD([[makeQuery(id+"F25.imprint","IMPRINT",EDGE,{"derivedFrom":sQuery(id+"F25.wireOp",EDGE,"E56.bottom")}),-1.0]])]});
            extrude(context, id + "F26", {"entities" : qUnion([Q0, Q1]), "operationType" : NewBodyOperationType.REMOVE, "oppositeDirection" : true, "depth" : 25 * mm});
        }
        {
            var Q0;
            Q0=makeQuery(id+"F24.imprint","IMPRINT",FACE,{"disambiguationData":[TD([[makeQuery(id+"F24.imprint","IMPRINT",EDGE,{"derivedFrom":sQuery(id+"F24.wireOp",EDGE,"E52.bottom")}),-1.0]])]});
            var Q1;
            Q1=makeQuery(id+"F24.imprint","IMPRINT",FACE,{"disambiguationData":[TD([[makeQuery(id+"F24.imprint","IMPRINT",EDGE,{"derivedFrom":sQuery(id+"F24.wireOp",EDGE,"E53.bottom")}),-1.0]])]});
            var Q2;
            Q2=makeQuery(id+"F24.imprint","IMPRINT",FACE,{"disambiguationData":[TD([[makeQuery(id+"F24.imprint","IMPRINT",EDGE,{"derivedFrom":sQuery(id+"F24.wireOp",EDGE,"E54.bottom")}),-1.0]])]});
            extrude(context, id + "F27", {"entities" : qUnion([Q0, Q1, Q2]), "operationType" : NewBodyOperationType.REMOVE, "oppositeDirection" : true, "depth" : 25 * mm});
        }
        {
            var Q0;
            Q0=makeQuery(id+"F23.boolean.opBoolean","COPY",EDGE,{"derivedFrom":makeQuery(id+"F23.opExtrude","SWEPT_EDGE",EDGE,{"disambiguationData":[OSD([sQuery(id+"F22.wireOp",EDGE,"E51.top"),sQuery(id+"F22.wireOp",EDGE,"E51.right")])]})});
            var Q1;
            Q1=makeQuery(id+"F23.boolean.opBoolean","COPY",EDGE,{"derivedFrom":makeQuery(id+"F23.opExtrude","SWEPT_EDGE",EDGE,{"disambiguationData":[OSD([sQuery(id+"F22.wireOp",EDGE,"E50.top"),sQuery(id+"F22.wireOp",EDGE,"E50.right")])]})});
            var Q2;
            Q2=makeQuery(id+"F23.boolean.opBoolean","COPY",EDGE,{"derivedFrom":makeQuery(id+"F23.opExtrude","SWEPT_EDGE",EDGE,{"disambiguationData":[OSD([sQuery(id+"F22.wireOp",EDGE,"E50.top"),sQuery(id+"F22.wireOp",EDGE,"E50.left")])]})});
            var Q3;
            Q3=makeQuery(id+"F23.boolean.opBoolean","COPY",EDGE,{"derivedFrom":makeQuery(id+"F23.opExtrude","SWEPT_EDGE",EDGE,{"disambiguationData":[OSD([sQuery(id+"F22.wireOp",EDGE,"E51.top"),sQuery(id+"F22.wireOp",EDGE,"E51.left")])]})});
            var Q4;
            Q4=makeQuery(id+"F23.boolean.opBoolean","COPY",EDGE,{"derivedFrom":makeQuery(id+"F23.opExtrude","SWEPT_EDGE",EDGE,{"disambiguationData":[OSD([sQuery(id+"F22.wireOp",EDGE,"E50.bottom"),sQuery(id+"F22.wireOp",EDGE,"E50.left")])]})});
            var Q5;
            Q5=makeQuery(id+"F23.boolean.opBoolean","COPY",EDGE,{"derivedFrom":makeQuery(id+"F23.opExtrude","SWEPT_EDGE",EDGE,{"disambiguationData":[OSD([sQuery(id+"F22.wireOp",EDGE,"E51.bottom"),sQuery(id+"F22.wireOp",EDGE,"E51.left")])]})});
            var Q6;
            Q6=makeQuery(id+"F23.boolean.opBoolean","COPY",EDGE,{"derivedFrom":makeQuery(id+"F23.opExtrude","SWEPT_EDGE",EDGE,{"disambiguationData":[OSD([sQuery(id+"F22.wireOp",EDGE,"E50.bottom"),sQuery(id+"F22.wireOp",EDGE,"E50.right")])]})});
            var Q7;
            Q7=makeQuery(id+"F23.boolean.opBoolean","COPY",EDGE,{"derivedFrom":makeQuery(id+"F23.opExtrude","SWEPT_EDGE",EDGE,{"disambiguationData":[OSD([sQuery(id+"F22.wireOp",EDGE,"E51.bottom"),sQuery(id+"F22.wireOp",EDGE,"E51.right")])]})});
            var Q8;
            Q8=makeQuery(id+"F8.opExtrude","SWEPT_FACE",FACE,{"disambiguationData":[OSD([sQuery(id+"F7.wireOp",EDGE,"E14.top")])]});
            var Q9;
            Q9=makeQuery(id+"F23.boolean.opBoolean","INTERSECT",EDGE,{"derivedFrom":[makeQuery(id+"F9.opShell","OFFSET_FACE",FACE,{"disambiguationData":[OSD([sQuery(id+"F7.wireOp",EDGE,"E14.top")])]}),makeQuery(id+"F23.opExtrude","SWEPT_FACE",FACE,{"disambiguationData":[OSD([sQuery(id+"F22.wireOp",EDGE,"QhVgcxdx-eRvb-omaO-OkVv-4pRQthqEzQQm.left")])]})]});
            var Q10;
            Q10=makeQuery(id+"F23.boolean.opBoolean","INTERSECT",EDGE,{"derivedFrom":[makeQuery(id+"F9.opShell","OFFSET_FACE",FACE,{"disambiguationData":[OSD([sQuery(id+"F7.wireOp",EDGE,"E14.top")])]}),makeQuery(id+"F23.opExtrude","SWEPT_FACE",FACE,{"disambiguationData":[OSD([sQuery(id+"F22.wireOp",EDGE,"E50.bottom")])]})]});
            var Q11;
            Q11=makeQuery(id+"F23.boolean.opBoolean","INTERSECT",EDGE,{"derivedFrom":[makeQuery(id+"F9.opShell","OFFSET_FACE",FACE,{"disambiguationData":[OSD([sQuery(id+"F7.wireOp",EDGE,"E14.top")])]}),makeQuery(id+"F23.opExtrude","SWEPT_FACE",FACE,{"disambiguationData":[OSD([sQuery(id+"F22.wireOp",EDGE,"E50.right")])]})]});
            var Q12;
            Q12=makeQuery(id+"F23.boolean.opBoolean","INTERSECT",EDGE,{"derivedFrom":[makeQuery(id+"F9.opShell","OFFSET_FACE",FACE,{"disambiguationData":[OSD([sQuery(id+"F7.wireOp",EDGE,"E14.top")])]}),makeQuery(id+"F23.opExtrude","SWEPT_FACE",FACE,{"disambiguationData":[OSD([sQuery(id+"F22.wireOp",EDGE,"E50.top")])]})]});
            var Q13;
            Q13=makeQuery(id+"F23.boolean.opBoolean","INTERSECT",EDGE,{"derivedFrom":[makeQuery(id+"F9.opShell","OFFSET_FACE",FACE,{"disambiguationData":[OSD([sQuery(id+"F7.wireOp",EDGE,"E14.top")])]}),makeQuery(id+"F23.opExtrude","SWEPT_FACE",FACE,{"disambiguationData":[OSD([sQuery(id+"F22.wireOp",EDGE,"E50.left")])]})]});
            var Q14;
            Q14=makeQuery(id+"F23.boolean.opBoolean","INTERSECT",EDGE,{"derivedFrom":[makeQuery(id+"F9.opShell","OFFSET_FACE",FACE,{"disambiguationData":[OSD([sQuery(id+"F7.wireOp",EDGE,"E14.top")])]}),makeQuery(id+"F23.opExtrude","SWEPT_FACE",FACE,{"disambiguationData":[OSD([sQuery(id+"F22.wireOp",EDGE,"E51.top")])]})]});
            var Q15;
            Q15=makeQuery(id+"F23.boolean.opBoolean","INTERSECT",EDGE,{"derivedFrom":[makeQuery(id+"F9.opShell","OFFSET_FACE",FACE,{"disambiguationData":[OSD([sQuery(id+"F7.wireOp",EDGE,"E14.top")])]}),makeQuery(id+"F23.opExtrude","SWEPT_FACE",FACE,{"disambiguationData":[OSD([sQuery(id+"F22.wireOp",EDGE,"E51.right")])]})]});
            var Q16;
            Q16=makeQuery(id+"F23.boolean.opBoolean","INTERSECT",EDGE,{"derivedFrom":[makeQuery(id+"F9.opShell","OFFSET_FACE",FACE,{"disambiguationData":[OSD([sQuery(id+"F7.wireOp",EDGE,"E14.top")])]}),makeQuery(id+"F23.opExtrude","SWEPT_FACE",FACE,{"disambiguationData":[OSD([sQuery(id+"F22.wireOp",EDGE,"E51.bottom")])]})]});
            var Q17;
            Q17=makeQuery(id+"F23.boolean.opBoolean","INTERSECT",EDGE,{"derivedFrom":[makeQuery(id+"F9.opShell","OFFSET_FACE",FACE,{"disambiguationData":[OSD([sQuery(id+"F7.wireOp",EDGE,"E14.top")])]}),makeQuery(id+"F23.opExtrude","SWEPT_FACE",FACE,{"disambiguationData":[OSD([sQuery(id+"F22.wireOp",EDGE,"E51.left")])]})]});
            var Q18;
            Q18=makeQuery(id+"F23.boolean.opBoolean","INTERSECT",EDGE,{"derivedFrom":[makeQuery(id+"F9.opShell","OFFSET_FACE",FACE,{"disambiguationData":[OSD([sQuery(id+"F7.wireOp",EDGE,"E14.top")])]}),makeQuery(id+"F23.opExtrude","SWEPT_FACE",FACE,{"disambiguationData":[OSD([sQuery(id+"F22.wireOp",EDGE,"sMDTSdTi-5NjA-m0rE-o88A-mWnj1oAAcxkY.bottom")])]})]});
            var Q19;
            Q19=makeQuery(id+"F23.boolean.opBoolean","INTERSECT",EDGE,{"derivedFrom":[makeQuery(id+"F9.opShell","OFFSET_FACE",FACE,{"disambiguationData":[OSD([sQuery(id+"F7.wireOp",EDGE,"E14.top")])]}),makeQuery(id+"F23.opExtrude","SWEPT_FACE",FACE,{"disambiguationData":[OSD([sQuery(id+"F22.wireOp",EDGE,"sMDTSdTi-5NjA-m0rE-o88A-mWnj1oAAcxkY.left")])]})]});
            var Q20;
            Q20=makeQuery(id+"F23.boolean.opBoolean","INTERSECT",EDGE,{"derivedFrom":[makeQuery(id+"F9.opShell","OFFSET_FACE",FACE,{"disambiguationData":[OSD([sQuery(id+"F7.wireOp",EDGE,"E14.top")])]}),makeQuery(id+"F23.opExtrude","SWEPT_FACE",FACE,{"disambiguationData":[OSD([sQuery(id+"F22.wireOp",EDGE,"sMDTSdTi-5NjA-m0rE-o88A-mWnj1oAAcxkY.top")])]})]});
            var Q21;
            Q21=makeQuery(id+"F23.boolean.opBoolean","INTERSECT",EDGE,{"derivedFrom":[makeQuery(id+"F9.opShell","OFFSET_FACE",FACE,{"disambiguationData":[OSD([sQuery(id+"F7.wireOp",EDGE,"E14.top")])]}),makeQuery(id+"F23.opExtrude","SWEPT_FACE",FACE,{"disambiguationData":[OSD([sQuery(id+"F22.wireOp",EDGE,"QhVgcxdx-eRvb-omaO-OkVv-4pRQthqEzQQm.top")])]})]});
            var Q22;
            Q22=makeQuery(id+"F23.boolean.opBoolean","INTERSECT",EDGE,{"derivedFrom":[makeQuery(id+"F9.opShell","OFFSET_FACE",FACE,{"disambiguationData":[OSD([sQuery(id+"F7.wireOp",EDGE,"E14.top")])]}),makeQuery(id+"F23.opExtrude","SWEPT_FACE",FACE,{"disambiguationData":[OSD([sQuery(id+"F22.wireOp",EDGE,"QhVgcxdx-eRvb-omaO-OkVv-4pRQthqEzQQm.bottom")])]})]});
            var Q23;
            Q23=makeQuery(id+"F23.boolean.opBoolean","INTERSECT",EDGE,{"derivedFrom":[makeQuery(id+"F9.opShell","OFFSET_FACE",FACE,{"disambiguationData":[OSD([sQuery(id+"F7.wireOp",EDGE,"E14.top")])]}),makeQuery(id+"F23.opExtrude","SWEPT_FACE",FACE,{"disambiguationData":[OSD([sQuery(id+"F22.wireOp",EDGE,"QhVgcxdx-eRvb-omaO-OkVv-4pRQthqEzQQm.right")])]})]});
            var Q24;
            Q24=makeQuery(id+"F23.boolean.opBoolean","INTERSECT",EDGE,{"derivedFrom":[makeQuery(id+"F9.opShell","OFFSET_FACE",FACE,{"disambiguationData":[OSD([sQuery(id+"F7.wireOp",EDGE,"E14.top")])]}),makeQuery(id+"F23.opExtrude","SWEPT_FACE",FACE,{"disambiguationData":[OSD([sQuery(id+"F22.wireOp",EDGE,"sMDTSdTi-5NjA-m0rE-o88A-mWnj1oAAcxkY.right")])]})]});
            var Q25;
            Q25=makeQuery(id+"F27.boolean.opBoolean","COPY",EDGE,{"derivedFrom":makeQuery(id+"F27.opExtrude","SWEPT_EDGE",EDGE,{"disambiguationData":[OSD([sQuery(id+"F24.wireOp",EDGE,"E52.top"),sQuery(id+"F24.wireOp",EDGE,"E52.left")])]})});
            var Q26;
            Q26=makeQuery(id+"F27.boolean.opBoolean","COPY",EDGE,{"derivedFrom":makeQuery(id+"F27.opExtrude","SWEPT_EDGE",EDGE,{"disambiguationData":[OSD([sQuery(id+"F24.wireOp",EDGE,"E52.top"),sQuery(id+"F24.wireOp",EDGE,"E52.right")])]})});
            var Q27;
            Q27=makeQuery(id+"F27.boolean.opBoolean","COPY",EDGE,{"derivedFrom":makeQuery(id+"F27.opExtrude","CAP_EDGE",EDGE,{"disambiguationData":[OSD([sQuery(id+"F24.wireOp",EDGE,"E52.top")])],"isStart":true})});
            var Q28;
            Q28=makeQuery(id+"F27.boolean.opBoolean","COPY",EDGE,{"derivedFrom":makeQuery(id+"F27.opExtrude","SWEPT_EDGE",EDGE,{"disambiguationData":[OSD([sQuery(id+"F24.wireOp",EDGE,"E52.bottom"),sQuery(id+"F24.wireOp",EDGE,"E52.right")])]})});
            var Q29;
            Q29=makeQuery(id+"F27.boolean.opBoolean","COPY",EDGE,{"derivedFrom":makeQuery(id+"F27.opExtrude","CAP_EDGE",EDGE,{"disambiguationData":[OSD([sQuery(id+"F24.wireOp",EDGE,"E52.right")])],"isStart":true})});
            var Q30;
            Q30=makeQuery(id+"F27.boolean.opBoolean","COPY",EDGE,{"derivedFrom":makeQuery(id+"F27.opExtrude","SWEPT_EDGE",EDGE,{"disambiguationData":[OSD([sQuery(id+"F24.wireOp",EDGE,"E52.bottom"),sQuery(id+"F24.wireOp",EDGE,"E52.left")])]})});
            var Q31;
            Q31=makeQuery(id+"F27.boolean.opBoolean","COPY",EDGE,{"derivedFrom":makeQuery(id+"F27.opExtrude","CAP_EDGE",EDGE,{"disambiguationData":[OSD([sQuery(id+"F24.wireOp",EDGE,"E52.left")])],"isStart":true})});
            var Q32;
            Q32=makeQuery(id+"F27.boolean.opBoolean","COPY",EDGE,{"derivedFrom":makeQuery(id+"F27.opExtrude","CAP_EDGE",EDGE,{"disambiguationData":[OSD([sQuery(id+"F24.wireOp",EDGE,"E52.bottom")])],"isStart":true})});
            var Q33;
            Q33=makeQuery(id+"F27.boolean.opBoolean","INTERSECT",EDGE,{"derivedFrom":[makeQuery(id+"F9.opShell","OFFSET_FACE",FACE,{"disambiguationData":[OSD([sQuery(id+"F7.wireOp",EDGE,"E14.bottom")])]}),makeQuery(id+"F27.opExtrude","SWEPT_FACE",FACE,{"disambiguationData":[OSD([sQuery(id+"F24.wireOp",EDGE,"E52.bottom")])]})]});
            var Q34;
            Q34=makeQuery(id+"F27.boolean.opBoolean","INTERSECT",EDGE,{"derivedFrom":[makeQuery(id+"F9.opShell","OFFSET_FACE",FACE,{"disambiguationData":[OSD([sQuery(id+"F7.wireOp",EDGE,"E14.bottom")])]}),makeQuery(id+"F27.opExtrude","SWEPT_FACE",FACE,{"disambiguationData":[OSD([sQuery(id+"F24.wireOp",EDGE,"E52.right")])]})]});
            var Q35;
            Q35=makeQuery(id+"F27.boolean.opBoolean","INTERSECT",EDGE,{"derivedFrom":[makeQuery(id+"F9.opShell","OFFSET_FACE",FACE,{"disambiguationData":[OSD([sQuery(id+"F7.wireOp",EDGE,"E14.bottom")])]}),makeQuery(id+"F27.opExtrude","SWEPT_FACE",FACE,{"disambiguationData":[OSD([sQuery(id+"F24.wireOp",EDGE,"E52.top")])]})]});
            var Q36;
            Q36=makeQuery(id+"F27.boolean.opBoolean","INTERSECT",EDGE,{"derivedFrom":[makeQuery(id+"F9.opShell","OFFSET_FACE",FACE,{"disambiguationData":[OSD([sQuery(id+"F7.wireOp",EDGE,"E14.bottom")])]}),makeQuery(id+"F27.opExtrude","SWEPT_FACE",FACE,{"disambiguationData":[OSD([sQuery(id+"F24.wireOp",EDGE,"E52.left")])]})]});
            var Q37;
            Q37=makeQuery(id+"F26.boolean.opBoolean","COPY",EDGE,{"derivedFrom":makeQuery(id+"F26.opExtrude","SWEPT_EDGE",EDGE,{"disambiguationData":[OSD([sQuery(id+"F25.wireOp",EDGE,"E55.top"),sQuery(id+"F25.wireOp",EDGE,"E55.right")])]})});
            var Q38;
            Q38=makeQuery(id+"F26.boolean.opBoolean","COPY",EDGE,{"derivedFrom":makeQuery(id+"F26.opExtrude","SWEPT_EDGE",EDGE,{"disambiguationData":[OSD([sQuery(id+"F25.wireOp",EDGE,"E56.top"),sQuery(id+"F25.wireOp",EDGE,"E56.right")])]})});
            var Q39;
            Q39=makeQuery(id+"F26.boolean.opBoolean","COPY",EDGE,{"derivedFrom":makeQuery(id+"F26.opExtrude","SWEPT_EDGE",EDGE,{"disambiguationData":[OSD([sQuery(id+"F25.wireOp",EDGE,"E56.top"),sQuery(id+"F25.wireOp",EDGE,"E56.left")])]})});
            var Q40;
            Q40=makeQuery(id+"F26.boolean.opBoolean","COPY",EDGE,{"derivedFrom":makeQuery(id+"F26.opExtrude","SWEPT_EDGE",EDGE,{"disambiguationData":[OSD([sQuery(id+"F25.wireOp",EDGE,"E55.top"),sQuery(id+"F25.wireOp",EDGE,"E55.left")])]})});
            var Q41;
            Q41=makeQuery(id+"F26.boolean.opBoolean","COPY",EDGE,{"derivedFrom":makeQuery(id+"F26.opExtrude","SWEPT_EDGE",EDGE,{"disambiguationData":[OSD([sQuery(id+"F25.wireOp",EDGE,"E56.bottom"),sQuery(id+"F25.wireOp",EDGE,"E56.left")])]})});
            var Q42;
            Q42=makeQuery(id+"F26.boolean.opBoolean","COPY",EDGE,{"derivedFrom":makeQuery(id+"F26.opExtrude","SWEPT_EDGE",EDGE,{"disambiguationData":[OSD([sQuery(id+"F25.wireOp",EDGE,"E55.bottom"),sQuery(id+"F25.wireOp",EDGE,"E55.left")])]})});
            var Q43;
            Q43=makeQuery(id+"F26.boolean.opBoolean","COPY",EDGE,{"derivedFrom":makeQuery(id+"F26.opExtrude","SWEPT_EDGE",EDGE,{"disambiguationData":[OSD([sQuery(id+"F25.wireOp",EDGE,"E55.bottom"),sQuery(id+"F25.wireOp",EDGE,"E55.right")])]})});
            var Q44;
            Q44=makeQuery(id+"F26.boolean.opBoolean","COPY",EDGE,{"derivedFrom":makeQuery(id+"F26.opExtrude","SWEPT_EDGE",EDGE,{"disambiguationData":[OSD([sQuery(id+"F25.wireOp",EDGE,"E56.bottom"),sQuery(id+"F25.wireOp",EDGE,"E56.right")])]})});
            var Q45;
            Q45=makeQuery(id+"F26.boolean.opBoolean","COPY",EDGE,{"derivedFrom":makeQuery(id+"F26.opExtrude","CAP_EDGE",EDGE,{"disambiguationData":[OSD([sQuery(id+"F25.wireOp",EDGE,"E56.bottom")])],"isStart":true})});
            var Q46;
            Q46=makeQuery(id+"F26.boolean.opBoolean","COPY",EDGE,{"derivedFrom":makeQuery(id+"F26.opExtrude","CAP_EDGE",EDGE,{"disambiguationData":[OSD([sQuery(id+"F25.wireOp",EDGE,"E55.bottom")])],"isStart":true})});
            var Q47;
            Q47=makeQuery(id+"F26.boolean.opBoolean","COPY",EDGE,{"derivedFrom":makeQuery(id+"F26.opExtrude","CAP_EDGE",EDGE,{"disambiguationData":[OSD([sQuery(id+"F25.wireOp",EDGE,"E55.left")])],"isStart":true})});
            var Q48;
            Q48=makeQuery(id+"F26.boolean.opBoolean","COPY",EDGE,{"derivedFrom":makeQuery(id+"F26.opExtrude","CAP_EDGE",EDGE,{"disambiguationData":[OSD([sQuery(id+"F25.wireOp",EDGE,"E55.top")])],"isStart":true})});
            var Q49;
            Q49=makeQuery(id+"F26.boolean.opBoolean","COPY",EDGE,{"derivedFrom":makeQuery(id+"F26.opExtrude","CAP_EDGE",EDGE,{"disambiguationData":[OSD([sQuery(id+"F25.wireOp",EDGE,"E55.right")])],"isStart":true})});
            var Q50;
            Q50=makeQuery(id+"F26.boolean.opBoolean","COPY",EDGE,{"derivedFrom":makeQuery(id+"F26.opExtrude","CAP_EDGE",EDGE,{"disambiguationData":[OSD([sQuery(id+"F25.wireOp",EDGE,"E56.left")])],"isStart":true})});
            var Q51;
            Q51=makeQuery(id+"F26.boolean.opBoolean","COPY",EDGE,{"derivedFrom":makeQuery(id+"F26.opExtrude","CAP_EDGE",EDGE,{"disambiguationData":[OSD([sQuery(id+"F25.wireOp",EDGE,"E56.top")])],"isStart":true})});
            var Q52;
            Q52=makeQuery(id+"F26.boolean.opBoolean","COPY",EDGE,{"derivedFrom":makeQuery(id+"F26.opExtrude","CAP_EDGE",EDGE,{"disambiguationData":[OSD([sQuery(id+"F25.wireOp",EDGE,"E56.right")])],"isStart":true})});
            var Q53;
            Q53=makeQuery(id+"F26.boolean.opBoolean","INTERSECT",EDGE,{"derivedFrom":[makeQuery(id+"F9.opShell","OFFSET_FACE",FACE,{"disambiguationData":[OSD([sQuery(id+"F7.wireOp",EDGE,"E14.right")])]}),makeQuery(id+"F26.opExtrude","SWEPT_FACE",FACE,{"disambiguationData":[OSD([sQuery(id+"F25.wireOp",EDGE,"E56.right")])]})]});
            var Q54;
            Q54=makeQuery(id+"F26.boolean.opBoolean","INTERSECT",EDGE,{"derivedFrom":[makeQuery(id+"F9.opShell","OFFSET_FACE",FACE,{"disambiguationData":[OSD([sQuery(id+"F7.wireOp",EDGE,"E14.right")])]}),makeQuery(id+"F26.opExtrude","SWEPT_FACE",FACE,{"disambiguationData":[OSD([sQuery(id+"F25.wireOp",EDGE,"E55.right")])]})]});
            var Q55;
            Q55=makeQuery(id+"F26.boolean.opBoolean","INTERSECT",EDGE,{"derivedFrom":[makeQuery(id+"F9.opShell","OFFSET_FACE",FACE,{"disambiguationData":[OSD([sQuery(id+"F7.wireOp",EDGE,"E14.right")])]}),makeQuery(id+"F26.opExtrude","SWEPT_FACE",FACE,{"disambiguationData":[OSD([sQuery(id+"F25.wireOp",EDGE,"E56.bottom")])]})]});
            var Q56;
            Q56=makeQuery(id+"F26.boolean.opBoolean","INTERSECT",EDGE,{"derivedFrom":[makeQuery(id+"F9.opShell","OFFSET_FACE",FACE,{"disambiguationData":[OSD([sQuery(id+"F7.wireOp",EDGE,"E14.right")])]}),makeQuery(id+"F26.opExtrude","SWEPT_FACE",FACE,{"disambiguationData":[OSD([sQuery(id+"F25.wireOp",EDGE,"E56.left")])]})]});
            var Q57;
            Q57=makeQuery(id+"F26.boolean.opBoolean","INTERSECT",EDGE,{"derivedFrom":[makeQuery(id+"F9.opShell","OFFSET_FACE",FACE,{"disambiguationData":[OSD([sQuery(id+"F7.wireOp",EDGE,"E14.right")])]}),makeQuery(id+"F26.opExtrude","SWEPT_FACE",FACE,{"disambiguationData":[OSD([sQuery(id+"F25.wireOp",EDGE,"E56.top")])]})]});
            var Q58;
            Q58=makeQuery(id+"F26.boolean.opBoolean","INTERSECT",EDGE,{"derivedFrom":[makeQuery(id+"F9.opShell","OFFSET_FACE",FACE,{"disambiguationData":[OSD([sQuery(id+"F7.wireOp",EDGE,"E14.right")])]}),makeQuery(id+"F26.opExtrude","SWEPT_FACE",FACE,{"disambiguationData":[OSD([sQuery(id+"F25.wireOp",EDGE,"E55.top")])]})]});
            var Q59;
            Q59=makeQuery(id+"F26.boolean.opBoolean","INTERSECT",EDGE,{"derivedFrom":[makeQuery(id+"F9.opShell","OFFSET_FACE",FACE,{"disambiguationData":[OSD([sQuery(id+"F7.wireOp",EDGE,"E14.right")])]}),makeQuery(id+"F26.opExtrude","SWEPT_FACE",FACE,{"disambiguationData":[OSD([sQuery(id+"F25.wireOp",EDGE,"E55.left")])]})]});
            var Q60;
            Q60=makeQuery(id+"F26.boolean.opBoolean","INTERSECT",EDGE,{"derivedFrom":[makeQuery(id+"F9.opShell","OFFSET_FACE",FACE,{"disambiguationData":[OSD([sQuery(id+"F7.wireOp",EDGE,"E14.right")])]}),makeQuery(id+"F26.opExtrude","SWEPT_FACE",FACE,{"disambiguationData":[OSD([sQuery(id+"F25.wireOp",EDGE,"E55.bottom")])]})]});
            var Q61;
            Q61=makeQuery(id+"F27.boolean.opBoolean","COPY",EDGE,{"derivedFrom":makeQuery(id+"F27.opExtrude","SWEPT_EDGE",EDGE,{"disambiguationData":[OSD([sQuery(id+"F24.wireOp",EDGE,"E53.bottom"),sQuery(id+"F24.wireOp",EDGE,"E53.left")])]})});
            var Q62;
            Q62=makeQuery(id+"F27.boolean.opBoolean","COPY",EDGE,{"derivedFrom":makeQuery(id+"F27.opExtrude","SWEPT_EDGE",EDGE,{"disambiguationData":[OSD([sQuery(id+"F24.wireOp",EDGE,"E53.bottom"),sQuery(id+"F24.wireOp",EDGE,"E53.right")])]})});
            var Q63;
            Q63=makeQuery(id+"F27.boolean.opBoolean","COPY",EDGE,{"derivedFrom":makeQuery(id+"F27.opExtrude","SWEPT_EDGE",EDGE,{"disambiguationData":[OSD([sQuery(id+"F24.wireOp",EDGE,"E53.top"),sQuery(id+"F24.wireOp",EDGE,"E53.right")])]})});
            var Q64;
            Q64=makeQuery(id+"F27.boolean.opBoolean","COPY",EDGE,{"derivedFrom":makeQuery(id+"F27.opExtrude","SWEPT_EDGE",EDGE,{"disambiguationData":[OSD([sQuery(id+"F24.wireOp",EDGE,"E53.top"),sQuery(id+"F24.wireOp",EDGE,"E53.left")])]})});
            var Q65;
            Q65=makeQuery(id+"F27.boolean.opBoolean","COPY",EDGE,{"derivedFrom":makeQuery(id+"F27.opExtrude","CAP_EDGE",EDGE,{"disambiguationData":[OSD([sQuery(id+"F24.wireOp",EDGE,"E53.left")])],"isStart":true})});
            var Q66;
            Q66=makeQuery(id+"F27.boolean.opBoolean","COPY",EDGE,{"derivedFrom":makeQuery(id+"F27.opExtrude","CAP_EDGE",EDGE,{"disambiguationData":[OSD([sQuery(id+"F24.wireOp",EDGE,"E53.bottom")])],"isStart":true})});
            var Q67;
            Q67=makeQuery(id+"F27.boolean.opBoolean","COPY",EDGE,{"derivedFrom":makeQuery(id+"F27.opExtrude","CAP_EDGE",EDGE,{"disambiguationData":[OSD([sQuery(id+"F24.wireOp",EDGE,"E53.top")])],"isStart":true})});
            var Q68;
            Q68=makeQuery(id+"F27.boolean.opBoolean","COPY",EDGE,{"derivedFrom":makeQuery(id+"F27.opExtrude","CAP_EDGE",EDGE,{"disambiguationData":[OSD([sQuery(id+"F24.wireOp",EDGE,"E53.right")])],"isStart":true})});
            var Q69;
            Q69=makeQuery(id+"F27.boolean.opBoolean","INTERSECT",EDGE,{"derivedFrom":[makeQuery(id+"F9.opShell","OFFSET_FACE",FACE,{"disambiguationData":[OSD([sQuery(id+"F7.wireOp",EDGE,"E14.bottom")])]}),makeQuery(id+"F27.opExtrude","SWEPT_FACE",FACE,{"disambiguationData":[OSD([sQuery(id+"F24.wireOp",EDGE,"E53.right")])]})]});
            var Q70;
            Q70=makeQuery(id+"F27.boolean.opBoolean","INTERSECT",EDGE,{"derivedFrom":[makeQuery(id+"F9.opShell","OFFSET_FACE",FACE,{"disambiguationData":[OSD([sQuery(id+"F7.wireOp",EDGE,"E14.bottom")])]}),makeQuery(id+"F27.opExtrude","SWEPT_FACE",FACE,{"disambiguationData":[OSD([sQuery(id+"F24.wireOp",EDGE,"E53.top")])]})]});
            var Q71;
            Q71=makeQuery(id+"F27.boolean.opBoolean","INTERSECT",EDGE,{"derivedFrom":[makeQuery(id+"F9.opShell","OFFSET_FACE",FACE,{"disambiguationData":[OSD([sQuery(id+"F7.wireOp",EDGE,"E14.bottom")])]}),makeQuery(id+"F27.opExtrude","SWEPT_FACE",FACE,{"disambiguationData":[OSD([sQuery(id+"F24.wireOp",EDGE,"E53.bottom")])]})]});
            var Q72;
            Q72=makeQuery(id+"F27.boolean.opBoolean","INTERSECT",EDGE,{"derivedFrom":[makeQuery(id+"F9.opShell","OFFSET_FACE",FACE,{"disambiguationData":[OSD([sQuery(id+"F7.wireOp",EDGE,"E14.bottom")])]}),makeQuery(id+"F27.opExtrude","SWEPT_FACE",FACE,{"disambiguationData":[OSD([sQuery(id+"F24.wireOp",EDGE,"E53.left")])]})]});
            var Q73;
            Q73=makeQuery(id+"F27.boolean.opBoolean","COPY",EDGE,{"derivedFrom":makeQuery(id+"F27.opExtrude","SWEPT_EDGE",EDGE,{"disambiguationData":[OSD([sQuery(id+"F24.wireOp",EDGE,"E54.bottom"),sQuery(id+"F24.wireOp",EDGE,"E54.right")])]})});
            var Q74;
            Q74=makeQuery(id+"F27.boolean.opBoolean","COPY",EDGE,{"derivedFrom":makeQuery(id+"F27.opExtrude","SWEPT_EDGE",EDGE,{"disambiguationData":[OSD([sQuery(id+"F24.wireOp",EDGE,"E54.bottom"),sQuery(id+"F24.wireOp",EDGE,"E54.left")])]})});
            var Q75;
            Q75=makeQuery(id+"F27.boolean.opBoolean","COPY",EDGE,{"derivedFrom":makeQuery(id+"F27.opExtrude","SWEPT_EDGE",EDGE,{"disambiguationData":[OSD([sQuery(id+"F24.wireOp",EDGE,"E54.top"),sQuery(id+"F24.wireOp",EDGE,"E54.left")])]})});
            var Q76;
            Q76=makeQuery(id+"F27.boolean.opBoolean","COPY",EDGE,{"derivedFrom":makeQuery(id+"F27.opExtrude","CAP_EDGE",EDGE,{"disambiguationData":[OSD([sQuery(id+"F24.wireOp",EDGE,"E54.left")])],"isStart":true})});
            var Q77;
            Q77=makeQuery(id+"F27.boolean.opBoolean","COPY",EDGE,{"derivedFrom":makeQuery(id+"F27.opExtrude","CAP_EDGE",EDGE,{"disambiguationData":[OSD([sQuery(id+"F24.wireOp",EDGE,"E54.bottom")])],"isStart":true})});
            var Q78;
            Q78=makeQuery(id+"F27.boolean.opBoolean","COPY",EDGE,{"derivedFrom":makeQuery(id+"F27.opExtrude","CAP_EDGE",EDGE,{"disambiguationData":[OSD([sQuery(id+"F24.wireOp",EDGE,"E54.top")])],"isStart":true})});
            var Q79;
            Q79=makeQuery(id+"F27.boolean.opBoolean","COPY",EDGE,{"derivedFrom":makeQuery(id+"F27.opExtrude","CAP_EDGE",EDGE,{"disambiguationData":[OSD([sQuery(id+"F24.wireOp",EDGE,"E54.right")])],"isStart":true})});
            var Q80;
            Q80=makeQuery(id+"F27.boolean.opBoolean","COPY",EDGE,{"derivedFrom":makeQuery(id+"F27.opExtrude","SWEPT_EDGE",EDGE,{"disambiguationData":[OSD([sQuery(id+"F24.wireOp",EDGE,"E54.top"),sQuery(id+"F24.wireOp",EDGE,"E54.right")])]})});
            var Q81;
            Q81=makeQuery(id+"F27.boolean.opBoolean","INTERSECT",EDGE,{"derivedFrom":[makeQuery(id+"F9.opShell","OFFSET_FACE",FACE,{"disambiguationData":[OSD([sQuery(id+"F7.wireOp",EDGE,"E14.bottom")])]}),makeQuery(id+"F27.opExtrude","SWEPT_FACE",FACE,{"disambiguationData":[OSD([sQuery(id+"F24.wireOp",EDGE,"E54.right")])]})]});
            var Q82;
            Q82=makeQuery(id+"F27.boolean.opBoolean","INTERSECT",EDGE,{"derivedFrom":[makeQuery(id+"F9.opShell","OFFSET_FACE",FACE,{"disambiguationData":[OSD([sQuery(id+"F7.wireOp",EDGE,"E14.bottom")])]}),makeQuery(id+"F27.opExtrude","SWEPT_FACE",FACE,{"disambiguationData":[OSD([sQuery(id+"F24.wireOp",EDGE,"E54.bottom")])]})]});
            var Q83;
            Q83=makeQuery(id+"F27.boolean.opBoolean","INTERSECT",EDGE,{"derivedFrom":[makeQuery(id+"F9.opShell","OFFSET_FACE",FACE,{"disambiguationData":[OSD([sQuery(id+"F7.wireOp",EDGE,"E14.bottom")])]}),makeQuery(id+"F27.opExtrude","SWEPT_FACE",FACE,{"disambiguationData":[OSD([sQuery(id+"F24.wireOp",EDGE,"E54.top")])]})]});
            var Q84;
            Q84=makeQuery(id+"F27.boolean.opBoolean","INTERSECT",EDGE,{"derivedFrom":[makeQuery(id+"F9.opShell","OFFSET_FACE",FACE,{"disambiguationData":[OSD([sQuery(id+"F7.wireOp",EDGE,"E14.bottom")])]}),makeQuery(id+"F27.opExtrude","SWEPT_FACE",FACE,{"disambiguationData":[OSD([sQuery(id+"F24.wireOp",EDGE,"E54.left")])]})]});
            fillet(context, id + "F28", {"entities" : qUnion([Q0, Q1, Q2, Q3, Q4, Q5, Q6, Q7, Q8, Q9, Q10, Q11, Q12, Q13, Q14, Q15, Q16, Q17, Q18, Q19, Q20, Q21, Q22, Q23, Q24, Q25, Q26, Q27, Q28, Q29, Q30, Q31, Q32, Q33, Q34, Q35, Q36, Q37, Q38, Q39, Q40, Q41, Q42, Q43, Q44, Q45, Q46, Q47, Q48, Q49, Q50, Q51, Q52, Q53, Q54, Q55, Q56, Q57, Q58, Q59, Q60, Q61, Q62, Q63, Q64, Q65, Q66, Q67, Q68, Q69, Q70, Q71, Q72, Q73, Q74, Q75, Q76, Q77, Q78, Q79, Q80, Q81, Q82, Q83, Q84]), "radius" : 1 * mm, "allowEdgeOverflow" : false});
        }
        {
            var Q0;
            {var subQ0=sQuery(id+"F7.wireOp",EDGE,"E14.left");var subQ1=sQuery(id+"F7.wireOp",EDGE,"E14.top");var subQ2=sQuery(id+"F7.wireOp",EDGE,"E14.right");var subQ3=sQuery(id+"F7.wireOp",EDGE,"E14.bottom");Q0=makeQuery(id+"F14.opBoolean","SPLIT",FACE,{"disambiguationData":[TD([makeQuery(id+"F4.opExtrude","SWEPT_FACE",FACE,{"disambiguationData":[OSD([sQuery(id+"F3.wireOp",EDGE,"E5")])]}),makeQuery(id+"F4.opExtrude","SWEPT_FACE",FACE,{"disambiguationData":[OSD([sQuery(id+"F3.wireOp",EDGE,"E6")])]}),makeQuery(id+"F4.opExtrude","SWEPT_FACE",FACE,{"disambiguationData":[OSD([sQuery(id+"F3.wireOp",EDGE,"E7")])]}),makeQuery(id+"F4.opExtrude","SWEPT_FACE",FACE,{"disambiguationData":[OSD([sQuery(id+"F3.wireOp",EDGE,"E8")])]}),makeQuery(id+"F6.opExtrude","SWEPT_FACE",FACE,{"disambiguationData":[OSD([sQuery(id+"F5.wireOp",EDGE,"E12")])]}),makeQuery(id+"F6.opExtrude","SWEPT_FACE",FACE,{"disambiguationData":[OSD([sQuery(id+"F5.wireOp",EDGE,"E13")])]}),makeQuery(id+"F9.opShell","OFFSET_FACE",FACE,{"disambiguationData":[OSD([subQ3])]}),makeQuery(id+"F9.opShell","OFFSET_FACE",FACE,{"disambiguationData":[OSD([subQ1])]}),makeQuery(id+"F9.opShell","OFFSET_FACE",FACE,{"disambiguationData":[OSD([subQ0])]}),makeQuery(id+"F9.opShell","OFFSET_FACE",FACE,{"disambiguationData":[OSD([subQ2])]}),makeQuery(id+"F10.opExtrude","SWEPT_FACE",FACE,{"disambiguationData":[OSD([sQuery(id+"F7.wireOp",EDGE,"E19")])]}),makeQuery(id+"F10.opExtrude","SWEPT_FACE",FACE,{"disambiguationData":[OSD([sQuery(id+"F7.wireOp",EDGE,"E20")])]}),makeQuery(id+"F10.opExtrude","SWEPT_FACE",FACE,{"disambiguationData":[OSD([sQuery(id+"F7.wireOp",EDGE,"E21")])]}),makeQuery(id+"F10.opExtrude","SWEPT_FACE",FACE,{"disambiguationData":[OSD([sQuery(id+"F7.wireOp",EDGE,"E22")])]})])],"derivedFrom":makeQuery(id+"F9.opShell","OFFSET_FACE",FACE,{"disambiguationData":[OSD([subQ3,subQ1,subQ0,subQ2])]})});}
            var sketch = newSketch(context, id + "F29", { "sketchPlane" : qUnion([Q0])});
            skLineSegment(sketch, "E57", {"start": v(-41.07, 89.6) * mm, "end": v(-41.07, 28.7) * mm});
            skLineSegment(sketch, "E58", {"start": v(-41.07, 28.7) * mm, "end": v(78.93, 28.7) * mm});
            skLineSegment(sketch, "E59", {"start": v(78.93, 28.7) * mm, "end": v(78.93, 61.2) * mm});
            skLineSegment(sketch, "E60", {"start": v(78.93, 61.2) * mm, "end": v(37.48, 61.2) * mm});
            skLineSegment(sketch, "E61", {"start": v(37.48, 61.2) * mm, "end": v(37.48, 89.6) * mm});
            skLineSegment(sketch, "E62", {"start": v(37.48, 89.6) * mm, "end": v(-41.07, 89.6) * mm});
            skLineSegment(sketch, "E63.bottom", {"start": v(78.93, 7.6) * mm, "end": v(-41.07, 7.6) * mm});
            skLineSegment(sketch, "E63.top", {"start": v(78.93, -25.4) * mm, "end": v(-41.07, -25.4) * mm});
            skLineSegment(sketch, "E63.left", {"start": v(78.93, 7.6) * mm, "end": v(78.93, -25.4) * mm});
            skLineSegment(sketch, "E63.right", {"start": v(-41.07, 7.6) * mm, "end": v(-41.07, -25.4) * mm});
            skLineSegment(sketch, "E64.bottom", {"start": v(36.38, -25.4) * mm, "end": v(78.93, -25.4) * mm});
            skLineSegment(sketch, "E64.top", {"start": v(36.38, -51.84) * mm, "end": v(78.93, -51.84) * mm});
            skLineSegment(sketch, "E64.left", {"start": v(36.38, -25.4) * mm, "end": v(36.38, -51.84) * mm});
            skLineSegment(sketch, "E64.right", {"start": v(78.93, -25.4) * mm, "end": v(78.93, -51.84) * mm});
            skLineSegment(sketch, "E65.bottom", {"start": v(57.48, 93.16) * mm, "end": v(78.93, 93.16) * mm});
            skLineSegment(sketch, "E65.top", {"start": v(57.48, 84.1) * mm, "end": v(78.93, 84.1) * mm});
            skLineSegment(sketch, "E65.left", {"start": v(57.48, 93.16) * mm, "end": v(57.48, 84.1) * mm});
            skLineSegment(sketch, "E65.right", {"start": v(78.93, 93.16) * mm, "end": v(78.93, 84.1) * mm});
            skSolve(sketch);
        }
        {
            var Q0;
            Q0=makeQuery(id+"F29.imprint","IMPRINT",FACE,{"disambiguationData":[TD([[makeQuery(id+"F29.imprint","IMPRINT",EDGE,{"derivedFrom":sQuery(id+"F29.wireOp",EDGE,"E57")}),1.0]])]});
            var Q1;
            Q1=makeQuery(id+"F29.imprint","IMPRINT",FACE,{"disambiguationData":[TD([[makeQuery(id+"F29.imprint","IMPRINT",EDGE,{"derivedFrom":sQuery(id+"F29.wireOp",EDGE,"E65.bottom")}),-1.0]])]});
            var Q2;
            Q2=makeQuery(id+"F29.imprint","IMPRINT",FACE,{"disambiguationData":[TD([[makeQuery(id+"F29.imprint","IMPRINT",EDGE,{"derivedFrom":sQuery(id+"F29.wireOp",EDGE,"E63.bottom")}),1.0]])]});
            var Q3;
            Q3=makeQuery(id+"F29.imprint","IMPRINT",FACE,{"disambiguationData":[TD([[makeQuery(id+"F29.imprint","IMPRINT",EDGE,{"derivedFrom":sQuery(id+"F29.wireOp",EDGE,"E64.bottom")}),-1.0]])]});
            extrude(context, id + "F30", {"entities" : qUnion([Q0, Q1, Q2, Q3]), "operationType" : NewBodyOperationType.REMOVE, "oppositeDirection" : true, "depth" : 25 * mm});
        }
        {
            var Q0;
            Q0=sQuery(id+"F5.wireOp",VERTEX,"E10");
            var Q1;
            Q1=sQuery(id+"F5.wireOp",VERTEX,"E11");
            var Q2;
            Q2=makeQuery(id+"F4.opExtrude","SWEPT_BODY",BODY,{"disambiguationData":[OSD([sQuery(id+"F3.wireOp",EDGE,"E5")])]});
            hole(context, id + "F31", {"style" : HoleStyle.SIMPLE, "endStyle" : HoleEndStyle.THROUGH, "oppositeDirection" : true, "holeDiameter" : 2.4 * mm, "tappedDepth" : 12 * mm, "tapClearance" : 3, "locations" : qUnion([Q0, Q1]), "scope" : qUnion([Q2])});
        }
        {
            var Q0;
            {var subQ0=sQuery(id+"F7.wireOp",EDGE,"E14.left");var subQ1=sQuery(id+"F7.wireOp",EDGE,"E14.top");var subQ2=sQuery(id+"F7.wireOp",EDGE,"E14.right");var subQ3=sQuery(id+"F7.wireOp",EDGE,"E14.bottom");Q0=makeQuery(id+"F14.opBoolean","SPLIT",FACE,{"disambiguationData":[TD([makeQuery(id+"F4.opExtrude","SWEPT_FACE",FACE,{"disambiguationData":[OSD([sQuery(id+"F3.wireOp",EDGE,"E5")])]}),makeQuery(id+"F4.opExtrude","SWEPT_FACE",FACE,{"disambiguationData":[OSD([sQuery(id+"F3.wireOp",EDGE,"E6")])]}),makeQuery(id+"F4.opExtrude","SWEPT_FACE",FACE,{"disambiguationData":[OSD([sQuery(id+"F3.wireOp",EDGE,"E7")])]}),makeQuery(id+"F4.opExtrude","SWEPT_FACE",FACE,{"disambiguationData":[OSD([sQuery(id+"F3.wireOp",EDGE,"E8")])]}),makeQuery(id+"F6.opExtrude","SWEPT_FACE",FACE,{"disambiguationData":[OSD([sQuery(id+"F5.wireOp",EDGE,"E12")])]}),makeQuery(id+"F6.opExtrude","SWEPT_FACE",FACE,{"disambiguationData":[OSD([sQuery(id+"F5.wireOp",EDGE,"E13")])]}),makeQuery(id+"F9.opShell","OFFSET_FACE",FACE,{"disambiguationData":[OSD([subQ3])]}),makeQuery(id+"F9.opShell","OFFSET_FACE",FACE,{"disambiguationData":[OSD([subQ1])]}),makeQuery(id+"F9.opShell","OFFSET_FACE",FACE,{"disambiguationData":[OSD([subQ0])]}),makeQuery(id+"F9.opShell","OFFSET_FACE",FACE,{"disambiguationData":[OSD([subQ2])]}),makeQuery(id+"F10.opExtrude","SWEPT_FACE",FACE,{"disambiguationData":[OSD([sQuery(id+"F7.wireOp",EDGE,"E19")])]}),makeQuery(id+"F10.opExtrude","SWEPT_FACE",FACE,{"disambiguationData":[OSD([sQuery(id+"F7.wireOp",EDGE,"E20")])]}),makeQuery(id+"F10.opExtrude","SWEPT_FACE",FACE,{"disambiguationData":[OSD([sQuery(id+"F7.wireOp",EDGE,"E21")])]}),makeQuery(id+"F10.opExtrude","SWEPT_FACE",FACE,{"disambiguationData":[OSD([sQuery(id+"F7.wireOp",EDGE,"E22")])]})])],"derivedFrom":makeQuery(id+"F9.opShell","OFFSET_FACE",FACE,{"disambiguationData":[OSD([subQ3,subQ1,subQ0,subQ2])]})});}
            var sketch = newSketch(context, id + "F32", { "sketchPlane" : qUnion([Q0])});
            skLineSegment(sketch, "E66.bottom", {"start": v(82.88, -48.1) * mm, "end": v(94.88, -48.1) * mm});
            skLineSegment(sketch, "E66.top", {"start": v(82.88, -40.6) * mm, "end": v(94.88, -40.6) * mm});
            skLineSegment(sketch, "E66.left", {"start": v(82.88, -48.1) * mm, "end": v(82.88, -40.6) * mm});
            skLineSegment(sketch, "E66.right", {"start": v(94.88, -48.1) * mm, "end": v(94.88, -40.6) * mm});
            skLineSegment(sketch, "E67.bottom", {"start": v(60.58, -63.84) * mm, "end": v(72.58, -63.84) * mm});
            skLineSegment(sketch, "E67.top", {"start": v(60.58, -56.34) * mm, "end": v(72.58, -56.34) * mm});
            skLineSegment(sketch, "E67.left", {"start": v(60.58, -63.84) * mm, "end": v(60.58, -56.34) * mm});
            skLineSegment(sketch, "E67.right", {"start": v(72.58, -63.84) * mm, "end": v(72.58, -56.34) * mm});
            skLineSegment(sketch, "E68.bottom", {"start": v(62.58, -65.51) * mm, "end": v(70.58, -65.51) * mm});
            skLineSegment(sketch, "E68.top", {"start": v(62.58, -52.32) * mm, "end": v(70.58, -52.32) * mm});
            skLineSegment(sketch, "E68.left", {"start": v(62.58, -65.51) * mm, "end": v(62.58, -52.32) * mm});
            skLineSegment(sketch, "E68.right", {"start": v(70.58, -65.51) * mm, "end": v(70.58, -52.32) * mm});
            skLineSegment(sketch, "E69.bottom", {"start": v(84.88, -50.7) * mm, "end": v(92.88, -50.7) * mm});
            skLineSegment(sketch, "E69.top", {"start": v(84.88, -35.88) * mm, "end": v(92.88, -35.88) * mm});
            skLineSegment(sketch, "E69.left", {"start": v(84.88, -50.7) * mm, "end": v(84.88, -35.88) * mm});
            skLineSegment(sketch, "E69.right", {"start": v(92.88, -50.7) * mm, "end": v(92.88, -35.88) * mm});
            skSolve(sketch);
        }
        {
            var Q0;
            {var subQ0=sQuery(id+"F32.wireOp",EDGE,"E67.left");Q0=makeQuery(id+"F32.imprint","IMPRINT",FACE,{"disambiguationData":[TD([[makeQuery(id+"F32.imprint","IMPRINT",EDGE,{"derivedFrom":subQ0}),-1.0]])]});}
            var Q1;
            {var subQ0=sQuery(id+"F32.wireOp",EDGE,"E68.left");var subQ1=sQuery(id+"F32.wireOp",EDGE,"E67.bottom");var subQ2=makeQuery(id+"F32.imprint","INTERSECT",VERTEX,{"derivedFrom":[subQ1,subQ0]});Q1=makeQuery(id+"F32.imprint","IMPRINT",FACE,{"disambiguationData":[TD([[makeQuery(id+"F32.imprint","IMPRINT",EDGE,{"disambiguationData":[TD([[subQ2,-1.0]])],"derivedFrom":subQ1}),1.0]])]});}
            var Q2;
            {var subQ0=sQuery(id+"F32.wireOp",EDGE,"E67.right");Q2=makeQuery(id+"F32.imprint","IMPRINT",FACE,{"disambiguationData":[TD([[makeQuery(id+"F32.imprint","IMPRINT",EDGE,{"derivedFrom":subQ0}),1.0]])]});}
            var Q3;
            {var subQ0=sQuery(id+"F32.wireOp",EDGE,"E66.left");Q3=makeQuery(id+"F32.imprint","IMPRINT",FACE,{"disambiguationData":[TD([[makeQuery(id+"F32.imprint","IMPRINT",EDGE,{"derivedFrom":subQ0}),-1.0]])]});}
            var Q4;
            {var subQ0=sQuery(id+"F32.wireOp",EDGE,"E69.left");var subQ1=sQuery(id+"F32.wireOp",EDGE,"E66.bottom");var subQ2=makeQuery(id+"F32.imprint","INTERSECT",VERTEX,{"derivedFrom":[subQ1,subQ0]});Q4=makeQuery(id+"F32.imprint","IMPRINT",FACE,{"disambiguationData":[TD([[makeQuery(id+"F32.imprint","IMPRINT",EDGE,{"disambiguationData":[TD([[subQ2,-1.0]])],"derivedFrom":subQ1}),1.0]])]});}
            var Q5;
            {var subQ0=sQuery(id+"F32.wireOp",EDGE,"E66.right");Q5=makeQuery(id+"F32.imprint","IMPRINT",FACE,{"disambiguationData":[TD([[makeQuery(id+"F32.imprint","IMPRINT",EDGE,{"derivedFrom":subQ0}),1.0]])]});}
            extrude(context, id + "F33", {"entities" : qUnion([Q0, Q1, Q2, Q3, Q4, Q5]), "operationType" : NewBodyOperationType.ADD, "depth" : 4 * mm});
        }
        {
            var Q0;
            {var subQ5=sQuery(id+"F32.wireOp",EDGE,"E68.bottom");Q0=makeQuery(id+"F32.imprint","IMPRINT",FACE,{"disambiguationData":[TD([[makeQuery(id+"F32.imprint","IMPRINT",EDGE,{"derivedFrom":subQ5}),1.0]])]});}
            var Q1;
            {var subQ0=sQuery(id+"F32.wireOp",EDGE,"E68.left");var subQ1=sQuery(id+"F32.wireOp",EDGE,"E67.bottom");var subQ2=makeQuery(id+"F32.imprint","INTERSECT",VERTEX,{"derivedFrom":[subQ1,subQ0]});Q1=makeQuery(id+"F32.imprint","IMPRINT",FACE,{"disambiguationData":[TD([[makeQuery(id+"F32.imprint","IMPRINT",EDGE,{"disambiguationData":[TD([[subQ2,-1.0]])],"derivedFrom":subQ1}),1.0]])]});}
            var Q2;
            {var subQ5=sQuery(id+"F32.wireOp",EDGE,"E68.top");Q2=makeQuery(id+"F32.imprint","IMPRINT",FACE,{"disambiguationData":[TD([[makeQuery(id+"F32.imprint","IMPRINT",EDGE,{"derivedFrom":subQ5}),-1.0]])]});}
            var Q3;
            {var subQ5=sQuery(id+"F32.wireOp",EDGE,"E69.bottom");Q3=makeQuery(id+"F32.imprint","IMPRINT",FACE,{"disambiguationData":[TD([[makeQuery(id+"F32.imprint","IMPRINT",EDGE,{"derivedFrom":subQ5}),1.0]])]});}
            var Q4;
            {var subQ0=sQuery(id+"F32.wireOp",EDGE,"E69.left");var subQ1=sQuery(id+"F32.wireOp",EDGE,"E66.bottom");var subQ2=makeQuery(id+"F32.imprint","INTERSECT",VERTEX,{"derivedFrom":[subQ1,subQ0]});Q4=makeQuery(id+"F32.imprint","IMPRINT",FACE,{"disambiguationData":[TD([[makeQuery(id+"F32.imprint","IMPRINT",EDGE,{"disambiguationData":[TD([[subQ2,-1.0]])],"derivedFrom":subQ1}),1.0]])]});}
            var Q5;
            {var subQ5=sQuery(id+"F32.wireOp",EDGE,"E69.top");Q5=makeQuery(id+"F32.imprint","IMPRINT",FACE,{"disambiguationData":[TD([[makeQuery(id+"F32.imprint","IMPRINT",EDGE,{"derivedFrom":subQ5}),-1.0]])]});}
            extrude(context, id + "F34", {"entities" : qUnion([Q0, Q1, Q2, Q3, Q4, Q5]), "operationType" : NewBodyOperationType.REMOVE, "depth" : 2 * mm});
        }
    });
